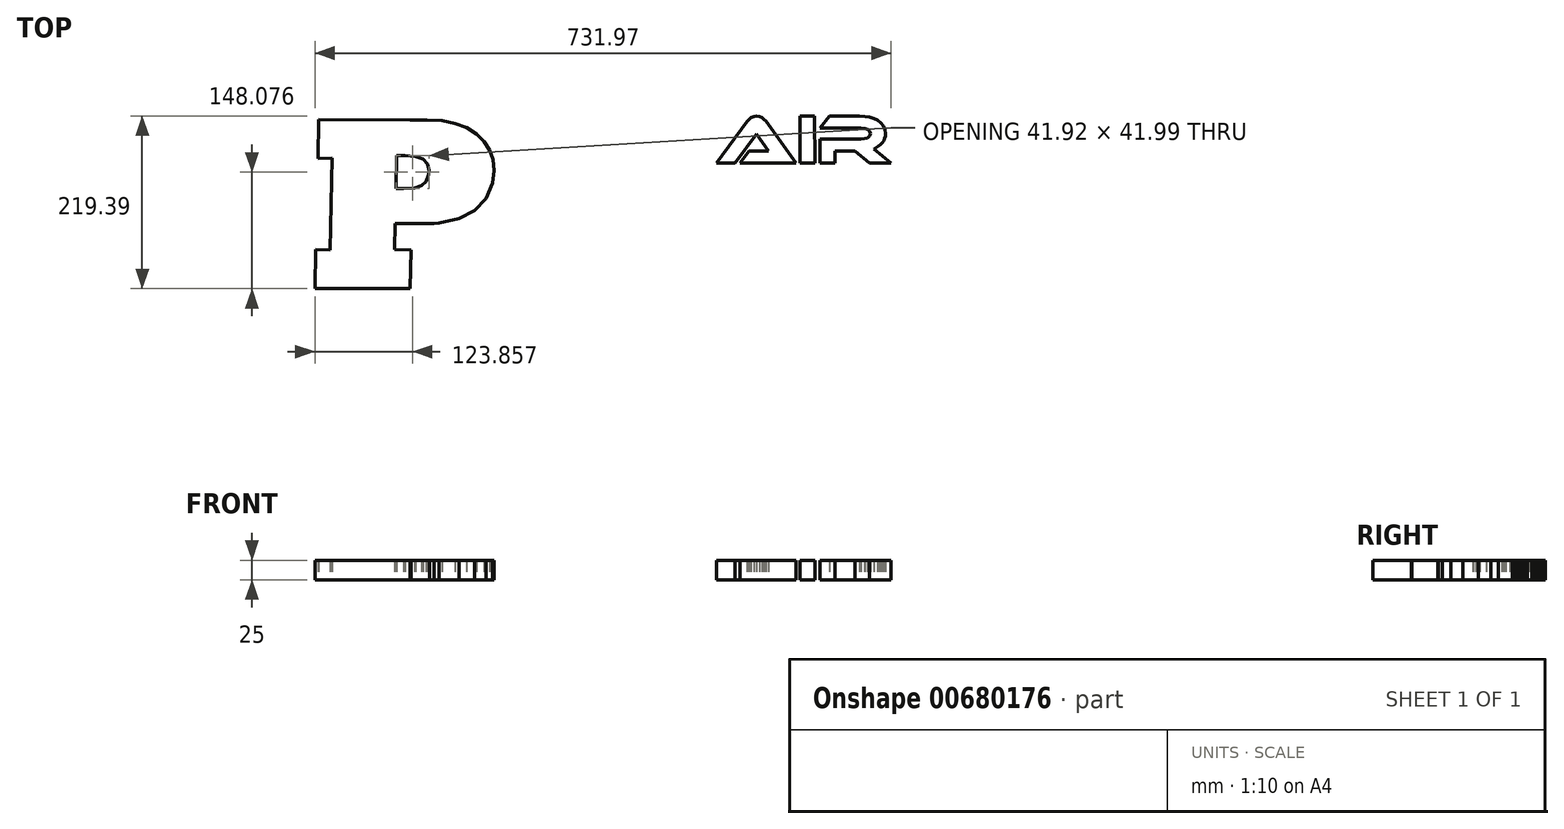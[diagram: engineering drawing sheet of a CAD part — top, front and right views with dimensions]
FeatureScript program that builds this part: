
annotation { "Feature Type Name" : "Feature", "Feature Type Description" : "" }
export const myFeature = defineFeature(function(context is Context, id is Id, definition is map)
    precondition{}
    {
        {
            var Q0;
            Q0=qCreatedBy(makeId("Top.planeOp"),FACE);
            var sketch = newSketch(context, id + "F0", { "sketchPlane" : qUnion([Q0])});
            skLineSegment(sketch, "E0", {"start": v(-203.38, -26.16) * mm, "end": v(-216.72, -33.2) * mm});
            skLineSegment(sketch, "E1", {"start": v(-216.72, -33.2) * mm, "end": v(-220.89, -34.75) * mm});
            skLineSegment(sketch, "E2", {"start": v(-220.89, -34.75) * mm, "end": v(-222.57, -34.45) * mm});
            skLineSegment(sketch, "E3", {"start": v(-222.57, -34.45) * mm, "end": v(-223.75, -33.54) * mm});
            skLineSegment(sketch, "E4", {"start": v(-223.75, -33.54) * mm, "end": v(-224.45, -31.99) * mm});
            skLineSegment(sketch, "E5", {"start": v(-224.45, -31.99) * mm, "end": v(-224.7, -29.77) * mm});
            skLineSegment(sketch, "E6", {"start": v(-224.7, -29.77) * mm, "end": v(-223.55, -23.02) * mm});
            skLineSegment(sketch, "E7", {"start": v(-223.55, -23.02) * mm, "end": v(-222.25, -19.7) * mm});
            skLineSegment(sketch, "E8", {"start": v(-222.25, -19.7) * mm, "end": v(-220.75, -17.4) * mm});
            skLineSegment(sketch, "E9", {"start": v(-220.75, -17.4) * mm, "end": v(-217.97, -15.19) * mm});
            skLineSegment(sketch, "E10", {"start": v(-217.97, -15.19) * mm, "end": v(-212.93, -12.27) * mm});
            skLineSegment(sketch, "E11", {"start": v(-212.93, -12.27) * mm, "end": v(-198.07, -5.72) * mm});
            skLineSegment(sketch, "E12", {"start": v(-198.07, -5.72) * mm, "end": v(-189.18, -2.7) * mm});
            skLineSegment(sketch, "E13", {"start": v(-189.18, -2.7) * mm, "end": v(-179.92, -0.26) * mm});
            skLineSegment(sketch, "E14", {"start": v(-179.92, -0.26) * mm, "end": v(-170.86, 1.37) * mm});
            skLineSegment(sketch, "E15", {"start": v(-170.86, 1.37) * mm, "end": v(-162.6, 1.92) * mm});
            skLineSegment(sketch, "E16", {"start": v(-162.6, 1.92) * mm, "end": v(-157.82, 1.48) * mm});
            skLineSegment(sketch, "E17", {"start": v(-157.82, 1.48) * mm, "end": v(-154.45, 0.18) * mm});
            skLineSegment(sketch, "E18", {"start": v(-154.45, 0.18) * mm, "end": v(-153.29, -1.05) * mm});
            skLineSegment(sketch, "E19", {"start": v(-153.29, -1.05) * mm, "end": v(-152.43, -2.99) * mm});
            skLineSegment(sketch, "E20", {"start": v(-152.43, -2.99) * mm, "end": v(-151.67, -9) * mm});
            skLineSegment(sketch, "E21", {"start": v(-151.67, -9) * mm, "end": v(-152.3, -13.27) * mm});
            skLineSegment(sketch, "E22", {"start": v(-152.3, -13.27) * mm, "end": v(-154.3, -17.99) * mm});
            skLineSegment(sketch, "E23", {"start": v(-154.3, -17.99) * mm, "end": v(-160.83, -27.6) * mm});
            skLineSegment(sketch, "E24", {"start": v(-160.83, -27.6) * mm, "end": v(-175.03, -44.15) * mm});
            skLineSegment(sketch, "E25", {"start": v(-175.03, -44.15) * mm, "end": v(-166.8, -43.03) * mm});
            skLineSegment(sketch, "E26", {"start": v(-166.8, -43.03) * mm, "end": v(-156.99, -41.97) * mm});
            skLineSegment(sketch, "E27", {"start": v(-156.99, -41.97) * mm, "end": v(-143.87, -22.9) * mm});
            skLineSegment(sketch, "E28", {"start": v(-143.87, -22.9) * mm, "end": v(-135.4, -11.09) * mm});
            skLineSegment(sketch, "E29", {"start": v(-135.4, -11.09) * mm, "end": v(-131.25, -5.72) * mm});
            skLineSegment(sketch, "E30", {"start": v(-131.25, -5.72) * mm, "end": v(-130.12, -4.73) * mm});
            skLineSegment(sketch, "E31", {"start": v(-130.12, -4.73) * mm, "end": v(-129.17, -4.63) * mm});
            skLineSegment(sketch, "E32", {"start": v(-129.17, -4.63) * mm, "end": v(-128.53, -5.44) * mm});
            skLineSegment(sketch, "E33", {"start": v(-128.53, -5.44) * mm, "end": v(-128.28, -7.2) * mm});
            skLineSegment(sketch, "E34", {"start": v(-128.28, -7.2) * mm, "end": v(-128.74, -11.37) * mm});
            skLineSegment(sketch, "E35", {"start": v(-128.74, -11.37) * mm, "end": v(-130.34, -14.57) * mm});
            skLineSegment(sketch, "E36", {"start": v(-130.34, -14.57) * mm, "end": v(-131.5, -16.28) * mm});
            skLineSegment(sketch, "E37", {"start": v(-131.5, -16.28) * mm, "end": v(-136.05, -23.27) * mm});
            skLineSegment(sketch, "E38", {"start": v(-136.05, -23.27) * mm, "end": v(-141.9, -31.82) * mm});
            skLineSegment(sketch, "E39", {"start": v(-141.9, -31.82) * mm, "end": v(-148.42, -41.85) * mm});
            skLineSegment(sketch, "E40", {"start": v(-148.42, -41.85) * mm, "end": v(-141.45, -42.42) * mm});
            skLineSegment(sketch, "E41", {"start": v(-141.45, -42.42) * mm, "end": v(-134.56, -43.65) * mm});
            skLineSegment(sketch, "E42", {"start": v(-134.56, -43.65) * mm, "end": v(-145.56, -58.86) * mm});
            skLineSegment(sketch, "E43", {"start": v(-145.56, -58.86) * mm, "end": v(-157.9, -58.24) * mm});
            skLineSegment(sketch, "E44", {"start": v(-157.9, -58.24) * mm, "end": v(-160.72, -64.1) * mm});
            skLineSegment(sketch, "E45", {"start": v(-160.72, -64.1) * mm, "end": v(-162.4, -68.13) * mm});
            skLineSegment(sketch, "E46", {"start": v(-162.4, -68.13) * mm, "end": v(-163.07, -71.66) * mm});
            skLineSegment(sketch, "E47", {"start": v(-163.07, -71.66) * mm, "end": v(-162.43, -74.31) * mm});
            skLineSegment(sketch, "E48", {"start": v(-162.43, -74.31) * mm, "end": v(-161.8, -76.22) * mm});
            skLineSegment(sketch, "E49", {"start": v(-161.8, -76.22) * mm, "end": v(-162.24, -77.5) * mm});
            skLineSegment(sketch, "E50", {"start": v(-162.24, -77.5) * mm, "end": v(-163.6, -78.88) * mm});
            skLineSegment(sketch, "E51", {"start": v(-163.6, -78.88) * mm, "end": v(-167.89, -81.34) * mm});
            skLineSegment(sketch, "E52", {"start": v(-167.89, -81.34) * mm, "end": v(-171.72, -82.4) * mm});
            skLineSegment(sketch, "E53", {"start": v(-171.72, -82.4) * mm, "end": v(-173.48, -81.53) * mm});
            skLineSegment(sketch, "E54", {"start": v(-173.48, -81.53) * mm, "end": v(-174.1, -78.9) * mm});
            skLineSegment(sketch, "E55", {"start": v(-174.1, -78.9) * mm, "end": v(-173.7, -74.93) * mm});
            skLineSegment(sketch, "E56", {"start": v(-173.7, -74.93) * mm, "end": v(-172.38, -70.24) * mm});
            skLineSegment(sketch, "E57", {"start": v(-172.38, -70.24) * mm, "end": v(-166.97, -58.74) * mm});
            skLineSegment(sketch, "E58", {"start": v(-166.97, -58.74) * mm, "end": v(-189.65, -61.67) * mm});
            skLineSegment(sketch, "E59", {"start": v(-189.65, -61.67) * mm, "end": v(-196.21, -70.9) * mm});
            skLineSegment(sketch, "E60", {"start": v(-196.21, -70.9) * mm, "end": v(-201.02, -78.28) * mm});
            skLineSegment(sketch, "E61", {"start": v(-201.02, -78.28) * mm, "end": v(-203.78, -82.28) * mm});
            skLineSegment(sketch, "E62", {"start": v(-203.78, -82.28) * mm, "end": v(-205.74, -83.28) * mm});
            skLineSegment(sketch, "E63", {"start": v(-205.74, -83.28) * mm, "end": v(-207.42, -82.89) * mm});
            skLineSegment(sketch, "E64", {"start": v(-207.42, -82.89) * mm, "end": v(-208.83, -81.72) * mm});
            skLineSegment(sketch, "E65", {"start": v(-208.83, -81.72) * mm, "end": v(-209.57, -80.47) * mm});
            skLineSegment(sketch, "E66", {"start": v(-209.57, -80.47) * mm, "end": v(-209.74, -79.1) * mm});
            skLineSegment(sketch, "E67", {"start": v(-209.74, -79.1) * mm, "end": v(-209.76, -77.78) * mm});
            skLineSegment(sketch, "E68", {"start": v(-209.76, -77.78) * mm, "end": v(-208.98, -75.6) * mm});
            skLineSegment(sketch, "E69", {"start": v(-208.98, -75.6) * mm, "end": v(-205.18, -69.88) * mm});
            skLineSegment(sketch, "E70", {"start": v(-205.18, -69.88) * mm, "end": v(-200.77, -63.42) * mm});
            skLineSegment(sketch, "E71", {"start": v(-200.77, -63.42) * mm, "end": v(-204.96, -63.6) * mm});
            skLineSegment(sketch, "E72", {"start": v(-204.96, -63.6) * mm, "end": v(-207.91, -63.3) * mm});
            skLineSegment(sketch, "E73", {"start": v(-207.91, -63.3) * mm, "end": v(-210.27, -62.42) * mm});
            skLineSegment(sketch, "E74", {"start": v(-210.27, -62.42) * mm, "end": v(-211.81, -61.1) * mm});
            skLineSegment(sketch, "E75", {"start": v(-211.81, -61.1) * mm, "end": v(-212.34, -59.49) * mm});
            skLineSegment(sketch, "E76", {"start": v(-212.34, -59.49) * mm, "end": v(-211.34, -55.21) * mm});
            skLineSegment(sketch, "E77", {"start": v(-211.34, -55.21) * mm, "end": v(-208.64, -51.41) * mm});
            skLineSegment(sketch, "E78", {"start": v(-208.64, -51.41) * mm, "end": v(-206.97, -50.27) * mm});
            skLineSegment(sketch, "E79", {"start": v(-206.97, -50.27) * mm, "end": v(-205.29, -49.88) * mm});
            skLineSegment(sketch, "E80", {"start": v(-205.29, -49.88) * mm, "end": v(-202.59, -50.57) * mm});
            skLineSegment(sketch, "E81", {"start": v(-202.59, -50.57) * mm, "end": v(-186.5, -46.58) * mm});
            skLineSegment(sketch, "E82", {"start": v(-186.5, -46.58) * mm, "end": v(-174.92, -33.54) * mm});
            skLineSegment(sketch, "E83", {"start": v(-174.92, -33.54) * mm, "end": v(-166.74, -23.55) * mm});
            skLineSegment(sketch, "E84", {"start": v(-166.74, -23.55) * mm, "end": v(-161.88, -16.6) * mm});
            skLineSegment(sketch, "E85", {"start": v(-161.88, -16.6) * mm, "end": v(-160.3, -12.67) * mm});
            skLineSegment(sketch, "E86", {"start": v(-160.3, -12.67) * mm, "end": v(-161.08, -10.4) * mm});
            skLineSegment(sketch, "E87", {"start": v(-161.08, -10.4) * mm, "end": v(-163.2, -9) * mm});
            skLineSegment(sketch, "E88", {"start": v(-163.2, -9) * mm, "end": v(-166.3, -8.51) * mm});
            skLineSegment(sketch, "E89", {"start": v(-166.3, -8.51) * mm, "end": v(-172.8, -9.63) * mm});
            skLineSegment(sketch, "E90", {"start": v(-172.8, -9.63) * mm, "end": v(-183.4, -12.92) * mm});
            skLineSegment(sketch, "E91", {"start": v(-183.4, -12.92) * mm, "end": v(-198.74, -18.95) * mm});
            skLineSegment(sketch, "E92", {"start": v(-198.74, -18.95) * mm, "end": v(-203.86, -21.24) * mm});
            skLineSegment(sketch, "E93", {"start": v(-203.86, -21.24) * mm, "end": v(-205.56, -22.5) * mm});
            skLineSegment(sketch, "E94", {"start": v(-205.56, -22.5) * mm, "end": v(-204.6, -23.61) * mm});
            skLineSegment(sketch, "E95", {"start": v(-204.6, -23.61) * mm, "end": v(-202.2, -23.99) * mm});
            skLineSegment(sketch, "E96", {"start": v(-202.2, -23.99) * mm, "end": v(-200.72, -24.42) * mm});
            skLineSegment(sketch, "E97", {"start": v(-200.72, -24.42) * mm, "end": v(-201.43, -25.1) * mm});
            skLineSegment(sketch, "E98", {"start": v(-201.43, -25.1) * mm, "end": v(-203.38, -26.16) * mm});
            skLineSegment(sketch, "E99", {"start": v(-126.25, -50.07) * mm, "end": v(-117.02, -42.58) * mm});
            skLineSegment(sketch, "E100", {"start": v(-117.02, -42.58) * mm, "end": v(-108.03, -37.3) * mm});
            skLineSegment(sketch, "E101", {"start": v(-108.03, -37.3) * mm, "end": v(-100.16, -34.17) * mm});
            skLineSegment(sketch, "E102", {"start": v(-100.16, -34.17) * mm, "end": v(-94.29, -33.13) * mm});
            skLineSegment(sketch, "E103", {"start": v(-94.29, -33.13) * mm, "end": v(-91.83, -34.22) * mm});
            skLineSegment(sketch, "E104", {"start": v(-91.83, -34.22) * mm, "end": v(-90, -36.74) * mm});
            skLineSegment(sketch, "E105", {"start": v(-90, -36.74) * mm, "end": v(-89.3, -38.86) * mm});
            skLineSegment(sketch, "E106", {"start": v(-89.3, -38.86) * mm, "end": v(-90.14, -40.5) * mm});
            skLineSegment(sketch, "E107", {"start": v(-90.14, -40.5) * mm, "end": v(-93.18, -41.78) * mm});
            skLineSegment(sketch, "E108", {"start": v(-93.18, -41.78) * mm, "end": v(-92, -44.34) * mm});
            skLineSegment(sketch, "E109", {"start": v(-92, -44.34) * mm, "end": v(-90.89, -46.86) * mm});
            skLineSegment(sketch, "E110", {"start": v(-90.89, -46.86) * mm, "end": v(-90.48, -48.58) * mm});
            skLineSegment(sketch, "E111", {"start": v(-90.48, -48.58) * mm, "end": v(-91.2, -50.72) * mm});
            skLineSegment(sketch, "E112", {"start": v(-91.2, -50.72) * mm, "end": v(-93.4, -54.16) * mm});
            skLineSegment(sketch, "E113", {"start": v(-93.4, -54.16) * mm, "end": v(-97.54, -60.18) * mm});
            skLineSegment(sketch, "E114", {"start": v(-97.54, -60.18) * mm, "end": v(-98.42, -62.33) * mm});
            skLineSegment(sketch, "E115", {"start": v(-98.42, -62.33) * mm, "end": v(-98.67, -64.92) * mm});
            skLineSegment(sketch, "E116", {"start": v(-98.67, -64.92) * mm, "end": v(-98.37, -66.94) * mm});
            skLineSegment(sketch, "E117", {"start": v(-98.37, -66.94) * mm, "end": v(-97.54, -68.38) * mm});
            skLineSegment(sketch, "E118", {"start": v(-97.54, -68.38) * mm, "end": v(-96.2, -69.25) * mm});
            skLineSegment(sketch, "E119", {"start": v(-96.2, -69.25) * mm, "end": v(-94.32, -69.54) * mm});
            skLineSegment(sketch, "E120", {"start": v(-94.32, -69.54) * mm, "end": v(-91.83, -69.03) * mm});
            skLineSegment(sketch, "E121", {"start": v(-91.83, -69.03) * mm, "end": v(-88.74, -67.5) * mm});
            skLineSegment(sketch, "E122", {"start": v(-80.77, -61.36) * mm, "end": v(-80.7, -65.17) * mm});
            skLineSegment(sketch, "E123", {"start": v(-87.9, -72.85) * mm, "end": v(-94.03, -78.33) * mm});
            skLineSegment(sketch, "E124", {"start": v(-94.03, -78.33) * mm, "end": v(-99.07, -81.63) * mm});
            skLineSegment(sketch, "E125", {"start": v(-99.07, -81.63) * mm, "end": v(-103.03, -82.72) * mm});
            skLineSegment(sketch, "E126", {"start": v(-103.03, -82.72) * mm, "end": v(-105.13, -82.33) * mm});
            skLineSegment(sketch, "E127", {"start": v(-105.13, -82.33) * mm, "end": v(-106.54, -81.13) * mm});
            skLineSegment(sketch, "E128", {"start": v(-106.54, -81.13) * mm, "end": v(-107.35, -79.15) * mm});
            skLineSegment(sketch, "E129", {"start": v(-107.35, -79.15) * mm, "end": v(-107.66, -76.41) * mm});
            skLineSegment(sketch, "E130", {"start": v(-107.66, -76.41) * mm, "end": v(-106.88, -70.37) * mm});
            skLineSegment(sketch, "E131", {"start": v(-106.88, -70.37) * mm, "end": v(-104.36, -62.11) * mm});
            skLineSegment(sketch, "E132", {"start": v(-104.36, -62.11) * mm, "end": v(-117.69, -76.5) * mm});
            skLineSegment(sketch, "E133", {"start": v(-117.69, -76.5) * mm, "end": v(-121.68, -79.72) * mm});
            skLineSegment(sketch, "E134", {"start": v(-121.68, -79.72) * mm, "end": v(-124.94, -80.79) * mm});
            skLineSegment(sketch, "E135", {"start": v(-124.94, -80.79) * mm, "end": v(-126.5, -80.2) * mm});
            skLineSegment(sketch, "E136", {"start": v(-126.5, -80.2) * mm, "end": v(-128.43, -78.4) * mm});
            skLineSegment(sketch, "E137", {"start": v(-128.43, -78.4) * mm, "end": v(-132.2, -72.26) * mm});
            skLineSegment(sketch, "E138", {"start": v(-132.2, -72.26) * mm, "end": v(-133.47, -68.4) * mm});
            skLineSegment(sketch, "E139", {"start": v(-133.47, -68.4) * mm, "end": v(-133.94, -64.42) * mm});
            skLineSegment(sketch, "E140", {"start": v(-133.94, -64.42) * mm, "end": v(-133.47, -59.52) * mm});
            skLineSegment(sketch, "E141", {"start": v(-133.47, -59.52) * mm, "end": v(-131.35, -55.5) * mm});
            skLineSegment(sketch, "E142", {"start": v(-131.35, -55.5) * mm, "end": v(-126.25, -50.07) * mm});
            skLineSegment(sketch, "E143", {"start": v(-96.4, -43.22) * mm, "end": v(-110.2, -50.07) * mm});
            skLineSegment(sketch, "E144", {"start": v(-110.2, -50.07) * mm, "end": v(-119.35, -55.8) * mm});
            skLineSegment(sketch, "E145", {"start": v(-119.35, -55.8) * mm, "end": v(-122.33, -58.42) * mm});
            skLineSegment(sketch, "E146", {"start": v(-122.33, -58.42) * mm, "end": v(-124.45, -61.06) * mm});
            skLineSegment(sketch, "E147", {"start": v(-124.45, -61.06) * mm, "end": v(-125.7, -63.75) * mm});
            skLineSegment(sketch, "E148", {"start": v(-125.7, -63.75) * mm, "end": v(-126.08, -66.48) * mm});
            skLineSegment(sketch, "E149", {"start": v(-126.08, -66.48) * mm, "end": v(-125.33, -69.76) * mm});
            skLineSegment(sketch, "E150", {"start": v(-125.33, -69.76) * mm, "end": v(-124.5, -70.72) * mm});
            skLineSegment(sketch, "E151", {"start": v(-124.5, -70.72) * mm, "end": v(-123.43, -71.04) * mm});
            skLineSegment(sketch, "E152", {"start": v(-123.43, -71.04) * mm, "end": v(-121, -70.16) * mm});
            skLineSegment(sketch, "E153", {"start": v(-121, -70.16) * mm, "end": v(-114.79, -65.7) * mm});
            skLineSegment(sketch, "E154", {"start": v(-114.79, -65.7) * mm, "end": v(-109.16, -60.08) * mm});
            skLineSegment(sketch, "E155", {"start": v(-109.16, -60.08) * mm, "end": v(-96.4, -43.22) * mm});
            skLineSegment(sketch, "E156", {"start": v(-39.37, -49.95) * mm, "end": v(-47.4, -60.32) * mm});
            skLineSegment(sketch, "E157", {"start": v(-47.4, -60.32) * mm, "end": v(-49.4, -64.11) * mm});
            skLineSegment(sketch, "E158", {"start": v(-49.4, -64.11) * mm, "end": v(-50.02, -66.98) * mm});
            skLineSegment(sketch, "E159", {"start": v(-50.02, -66.98) * mm, "end": v(-49.43, -69) * mm});
            skLineSegment(sketch, "E160", {"start": v(-49.43, -69) * mm, "end": v(-47.77, -69.67) * mm});
            skLineSegment(sketch, "E161", {"start": v(-47.77, -69.67) * mm, "end": v(-45.69, -69.2) * mm});
            skLineSegment(sketch, "E162", {"start": v(-45.69, -69.2) * mm, "end": v(-43.08, -67.76) * mm});
            skLineSegment(sketch, "E163", {"start": v(-34.12, -60.99) * mm, "end": v(-34.02, -65.3) * mm});
            skLineSegment(sketch, "E164", {"start": v(-47.4, -77.92) * mm, "end": v(-51.66, -80.82) * mm});
            skLineSegment(sketch, "E165", {"start": v(-51.66, -80.82) * mm, "end": v(-55.1, -81.8) * mm});
            skLineSegment(sketch, "E166", {"start": v(-55.1, -81.8) * mm, "end": v(-57.35, -81.37) * mm});
            skLineSegment(sketch, "E167", {"start": v(-57.35, -81.37) * mm, "end": v(-58.98, -80.1) * mm});
            skLineSegment(sketch, "E168", {"start": v(-58.98, -80.1) * mm, "end": v(-60, -78) * mm});
            skLineSegment(sketch, "E169", {"start": v(-60, -78) * mm, "end": v(-60.37, -75.04) * mm});
            skLineSegment(sketch, "E170", {"start": v(-60.37, -75.04) * mm, "end": v(-59.83, -71.1) * mm});
            skLineSegment(sketch, "E171", {"start": v(-59.83, -71.1) * mm, "end": v(-58.2, -67.08) * mm});
            skLineSegment(sketch, "E172", {"start": v(-58.2, -67.08) * mm, "end": v(-54.97, -61.08) * mm});
            skLineSegment(sketch, "E173", {"start": v(-54.97, -61.08) * mm, "end": v(-49.96, -52.26) * mm});
            skLineSegment(sketch, "E174", {"start": v(-49.96, -52.26) * mm, "end": v(-53.93, -54.95) * mm});
            skLineSegment(sketch, "E175", {"start": v(-53.93, -54.95) * mm, "end": v(-58.76, -59.43) * mm});
            skLineSegment(sketch, "E176", {"start": v(-58.76, -59.43) * mm, "end": v(-64.58, -65.83) * mm});
            skLineSegment(sketch, "E177", {"start": v(-64.58, -65.83) * mm, "end": v(-69.67, -72.57) * mm});
            skLineSegment(sketch, "E178", {"start": v(-69.67, -72.57) * mm, "end": v(-73.64, -77.57) * mm});
            skLineSegment(sketch, "E179", {"start": v(-73.64, -77.57) * mm, "end": v(-74.91, -78.53) * mm});
            skLineSegment(sketch, "E180", {"start": v(-74.91, -78.53) * mm, "end": v(-76.21, -78.85) * mm});
            skLineSegment(sketch, "E181", {"start": v(-76.21, -78.85) * mm, "end": v(-78.16, -77.8) * mm});
            skLineSegment(sketch, "E182", {"start": v(-78.16, -77.8) * mm, "end": v(-80, -74.66) * mm});
            skLineSegment(sketch, "E183", {"start": v(-80, -74.66) * mm, "end": v(-81.36, -70.13) * mm});
            skLineSegment(sketch, "E184", {"start": v(-81.21, -59.55) * mm, "end": v(-78.23, -54.06) * mm});
            skLineSegment(sketch, "E185", {"start": v(-78.23, -54.06) * mm, "end": v(-74.32, -48.33) * mm});
            skLineSegment(sketch, "E186", {"start": v(-74.32, -48.33) * mm, "end": v(-70.98, -44.37) * mm});
            skLineSegment(sketch, "E187", {"start": v(-70.98, -44.37) * mm, "end": v(-67.96, -42.06) * mm});
            skLineSegment(sketch, "E188", {"start": v(-67.96, -42.06) * mm, "end": v(-65.03, -41.29) * mm});
            skLineSegment(sketch, "E189", {"start": v(-65.03, -41.29) * mm, "end": v(-61.8, -41.97) * mm});
            skLineSegment(sketch, "E190", {"start": v(-61.8, -41.97) * mm, "end": v(-60.86, -42.84) * mm});
            skLineSegment(sketch, "E191", {"start": v(-60.86, -42.84) * mm, "end": v(-60.53, -44.09) * mm});
            skLineSegment(sketch, "E192", {"start": v(-60.53, -44.09) * mm, "end": v(-60.88, -45.4) * mm});
            skLineSegment(sketch, "E193", {"start": v(-60.88, -45.4) * mm, "end": v(-61.7, -46.64) * mm});
            skLineSegment(sketch, "E194", {"start": v(-61.7, -46.64) * mm, "end": v(-63.62, -48.83) * mm});
            skLineSegment(sketch, "E195", {"start": v(-63.62, -48.83) * mm, "end": v(-70.85, -57.82) * mm});
            skLineSegment(sketch, "E196", {"start": v(-70.85, -57.82) * mm, "end": v(-72.65, -60.88) * mm});
            skLineSegment(sketch, "E197", {"start": v(-72.65, -60.88) * mm, "end": v(-73.22, -62.99) * mm});
            skLineSegment(sketch, "E198", {"start": v(-73.22, -62.99) * mm, "end": v(-72.9, -64.34) * mm});
            skLineSegment(sketch, "E199", {"start": v(-72.9, -64.34) * mm, "end": v(-72, -64.8) * mm});
            skLineSegment(sketch, "E200", {"start": v(-72, -64.8) * mm, "end": v(-69.13, -62.4) * mm});
            skLineSegment(sketch, "E201", {"start": v(-69.13, -62.4) * mm, "end": v(-63.69, -56.1) * mm});
            skLineSegment(sketch, "E202", {"start": v(-63.69, -56.1) * mm, "end": v(-55.79, -47.95) * mm});
            skLineSegment(sketch, "E203", {"start": v(-55.79, -47.95) * mm, "end": v(-45.35, -39.8) * mm});
            skLineSegment(sketch, "E204", {"start": v(-45.35, -39.8) * mm, "end": v(-42.36, -38.06) * mm});
            skLineSegment(sketch, "E205", {"start": v(-42.36, -38.06) * mm, "end": v(-39.9, -37.49) * mm});
            skLineSegment(sketch, "E206", {"start": v(-39.9, -37.49) * mm, "end": v(-38.89, -38.17) * mm});
            skLineSegment(sketch, "E207", {"start": v(-38.89, -38.17) * mm, "end": v(-37.87, -40.23) * mm});
            skLineSegment(sketch, "E208", {"start": v(-37.87, -40.23) * mm, "end": v(-36.77, -45.77) * mm});
            skLineSegment(sketch, "E209", {"start": v(-36.77, -45.77) * mm, "end": v(-37.4, -47.5) * mm});
            skLineSegment(sketch, "E210", {"start": v(-37.4, -47.5) * mm, "end": v(-39.37, -49.95) * mm});
            skLineSegment(sketch, "E211", {"start": v(-4.98, -82.48) * mm, "end": v(-13.06, -95.7) * mm});
            skLineSegment(sketch, "E212", {"start": v(-13.06, -95.7) * mm, "end": v(-20.45, -105.11) * mm});
            skLineSegment(sketch, "E213", {"start": v(-20.45, -105.11) * mm, "end": v(-26.61, -110.73) * mm});
            skLineSegment(sketch, "E214", {"start": v(-26.61, -110.73) * mm, "end": v(-29.03, -112.13) * mm});
            skLineSegment(sketch, "E215", {"start": v(-29.03, -112.13) * mm, "end": v(-31.01, -112.6) * mm});
            skLineSegment(sketch, "E216", {"start": v(-31.01, -112.6) * mm, "end": v(-32.44, -112.02) * mm});
            skLineSegment(sketch, "E217", {"start": v(-32.44, -112.02) * mm, "end": v(-32.95, -110.28) * mm});
            skLineSegment(sketch, "E218", {"start": v(-32.95, -110.28) * mm, "end": v(-31.92, -105.14) * mm});
            skLineSegment(sketch, "E219", {"start": v(-31.92, -105.14) * mm, "end": v(-28.63, -98.75) * mm});
            skLineSegment(sketch, "E220", {"start": v(-28.63, -98.75) * mm, "end": v(-24.58, -93.37) * mm});
            skLineSegment(sketch, "E221", {"start": v(-24.58, -93.37) * mm, "end": v(-20.23, -88.83) * mm});
            skLineSegment(sketch, "E222", {"start": v(-20.23, -88.83) * mm, "end": v(-14.79, -84.08) * mm});
            skLineSegment(sketch, "E223", {"start": v(-14.79, -84.08) * mm, "end": v(-10.17, -80.17) * mm});
            skLineSegment(sketch, "E224", {"start": v(-10.17, -80.17) * mm, "end": v(-1.61, -60.68) * mm});
            skLineSegment(sketch, "E225", {"start": v(-1.61, -60.68) * mm, "end": v(-11.64, -70.92) * mm});
            skLineSegment(sketch, "E226", {"start": v(-11.64, -70.92) * mm, "end": v(-19.56, -77.07) * mm});
            skLineSegment(sketch, "E227", {"start": v(-19.56, -77.07) * mm, "end": v(-23, -78.7) * mm});
            skLineSegment(sketch, "E228", {"start": v(-23, -78.7) * mm, "end": v(-26.12, -79.23) * mm});
            skLineSegment(sketch, "E229", {"start": v(-26.12, -79.23) * mm, "end": v(-27.7, -78.91) * mm});
            skLineSegment(sketch, "E230", {"start": v(-27.7, -78.91) * mm, "end": v(-29.22, -77.96) * mm});
            skLineSegment(sketch, "E231", {"start": v(-29.22, -77.96) * mm, "end": v(-32.13, -74.14) * mm});
            skLineSegment(sketch, "E232", {"start": v(-32.13, -74.14) * mm, "end": v(-34.27, -68.97) * mm});
            skLineSegment(sketch, "E233", {"start": v(-34.02, -58.43) * mm, "end": v(-30.52, -52.57) * mm});
            skLineSegment(sketch, "E234", {"start": v(-30.52, -52.57) * mm, "end": v(-24.37, -46.18) * mm});
            skLineSegment(sketch, "E235", {"start": v(-24.37, -46.18) * mm, "end": v(-15.57, -39.8) * mm});
            skLineSegment(sketch, "E236", {"start": v(-15.57, -39.8) * mm, "end": v(-7.05, -35.26) * mm});
            skLineSegment(sketch, "E237", {"start": v(-7.05, -35.26) * mm, "end": v(-3.58, -34.13) * mm});
            skLineSegment(sketch, "E238", {"start": v(-3.58, -34.13) * mm, "end": v(-0.63, -33.75) * mm});
            skLineSegment(sketch, "E239", {"start": v(-0.63, -33.75) * mm, "end": v(2.4, -34.48) * mm});
            skLineSegment(sketch, "E240", {"start": v(2.4, -34.48) * mm, "end": v(3.17, -35.4) * mm});
            skLineSegment(sketch, "E241", {"start": v(3.17, -35.4) * mm, "end": v(3.45, -36.68) * mm});
            skLineSegment(sketch, "E242", {"start": v(3.45, -36.68) * mm, "end": v(2.95, -38.69) * mm});
            skLineSegment(sketch, "E243", {"start": v(2.95, -38.69) * mm, "end": v(1.37, -40.68) * mm});
            skLineSegment(sketch, "E244", {"start": v(1.37, -40.68) * mm, "end": v(-1.3, -42.64) * mm});
            skLineSegment(sketch, "E245", {"start": v(-1.3, -42.64) * mm, "end": v(-5.06, -44.59) * mm});
            skLineSegment(sketch, "E246", {"start": v(-5.06, -44.59) * mm, "end": v(-10.3, -47.27) * mm});
            skLineSegment(sketch, "E247", {"start": v(-10.3, -47.27) * mm, "end": v(-15.47, -50.7) * mm});
            skLineSegment(sketch, "E248", {"start": v(-15.47, -50.7) * mm, "end": v(-20.1, -54.62) * mm});
            skLineSegment(sketch, "E249", {"start": v(-20.1, -54.62) * mm, "end": v(-23.74, -58.77) * mm});
            skLineSegment(sketch, "E250", {"start": v(-23.74, -58.77) * mm, "end": v(-26.06, -62.84) * mm});
            skLineSegment(sketch, "E251", {"start": v(-26.06, -62.84) * mm, "end": v(-26.79, -66.48) * mm});
            skLineSegment(sketch, "E252", {"start": v(-26.79, -66.48) * mm, "end": v(-25.91, -69.17) * mm});
            skLineSegment(sketch, "E253", {"start": v(-25.91, -69.17) * mm, "end": v(-23.76, -70.17) * mm});
            skLineSegment(sketch, "E254", {"start": v(-23.76, -70.17) * mm, "end": v(-21.42, -69.67) * mm});
            skLineSegment(sketch, "E255", {"start": v(-21.42, -69.67) * mm, "end": v(-18.8, -68.17) * mm});
            skLineSegment(sketch, "E256", {"start": v(-18.8, -68.17) * mm, "end": v(-10.62, -61.12) * mm});
            skLineSegment(sketch, "E257", {"start": v(-10.62, -61.12) * mm, "end": v(-4.13, -53.66) * mm});
            skLineSegment(sketch, "E258", {"start": v(-4.13, -53.66) * mm, "end": v(2.57, -45.8) * mm});
            skLineSegment(sketch, "E259", {"start": v(2.57, -45.8) * mm, "end": v(5.11, -43.77) * mm});
            skLineSegment(sketch, "E260", {"start": v(5.11, -43.77) * mm, "end": v(7.42, -43.1) * mm});
            skLineSegment(sketch, "E261", {"start": v(7.42, -43.1) * mm, "end": v(9.47, -43.87) * mm});
            skLineSegment(sketch, "E262", {"start": v(9.47, -43.87) * mm, "end": v(10.31, -46.15) * mm});
            skLineSegment(sketch, "E263", {"start": v(10.31, -46.15) * mm, "end": v(9.83, -49.66) * mm});
            skLineSegment(sketch, "E264", {"start": v(9.83, -49.66) * mm, "end": v(8.23, -54.47) * mm});
            skLineSegment(sketch, "E265", {"start": v(8.23, -54.47) * mm, "end": v(0.42, -72.36) * mm});
            skLineSegment(sketch, "E266", {"start": v(15.32, -61.37) * mm, "end": v(15.42, -65.42) * mm});
            skLineSegment(sketch, "E267", {"start": v(21.93, -50.07) * mm, "end": v(31.12, -42.58) * mm});
            skLineSegment(sketch, "E268", {"start": v(31.12, -42.58) * mm, "end": v(40.08, -37.3) * mm});
            skLineSegment(sketch, "E269", {"start": v(40.08, -37.3) * mm, "end": v(47.93, -34.17) * mm});
            skLineSegment(sketch, "E270", {"start": v(47.93, -34.17) * mm, "end": v(53.8, -33.13) * mm});
            skLineSegment(sketch, "E271", {"start": v(53.8, -33.13) * mm, "end": v(56.27, -34.21) * mm});
            skLineSegment(sketch, "E272", {"start": v(56.27, -34.21) * mm, "end": v(58.12, -36.74) * mm});
            skLineSegment(sketch, "E273", {"start": v(58.12, -36.74) * mm, "end": v(58.83, -38.85) * mm});
            skLineSegment(sketch, "E274", {"start": v(58.83, -38.85) * mm, "end": v(58, -40.5) * mm});
            skLineSegment(sketch, "E275", {"start": v(58, -40.5) * mm, "end": v(54.97, -41.78) * mm});
            skLineSegment(sketch, "E276", {"start": v(54.97, -41.78) * mm, "end": v(56.16, -44.34) * mm});
            skLineSegment(sketch, "E277", {"start": v(56.16, -44.34) * mm, "end": v(57.3, -46.86) * mm});
            skLineSegment(sketch, "E278", {"start": v(57.3, -46.86) * mm, "end": v(57.71, -48.58) * mm});
            skLineSegment(sketch, "E279", {"start": v(57.71, -48.58) * mm, "end": v(57.01, -50.72) * mm});
            skLineSegment(sketch, "E280", {"start": v(57.01, -50.72) * mm, "end": v(54.82, -54.16) * mm});
            skLineSegment(sketch, "E281", {"start": v(54.82, -54.16) * mm, "end": v(50.72, -60.18) * mm});
            skLineSegment(sketch, "E282", {"start": v(50.72, -60.18) * mm, "end": v(49.86, -62.33) * mm});
            skLineSegment(sketch, "E283", {"start": v(49.86, -62.33) * mm, "end": v(49.63, -64.93) * mm});
            skLineSegment(sketch, "E284", {"start": v(49.63, -64.93) * mm, "end": v(49.94, -66.95) * mm});
            skLineSegment(sketch, "E285", {"start": v(49.94, -66.95) * mm, "end": v(50.78, -68.4) * mm});
            skLineSegment(sketch, "E286", {"start": v(50.78, -68.4) * mm, "end": v(52.14, -69.26) * mm});
            skLineSegment(sketch, "E287", {"start": v(52.14, -69.26) * mm, "end": v(54, -69.55) * mm});
            skLineSegment(sketch, "E288", {"start": v(54, -69.55) * mm, "end": v(56.5, -69.04) * mm});
            skLineSegment(sketch, "E289", {"start": v(56.5, -69.04) * mm, "end": v(59.58, -67.5) * mm});
            skLineSegment(sketch, "E290", {"start": v(67.62, -65.18) * mm, "end": v(60.46, -72.86) * mm});
            skLineSegment(sketch, "E291", {"start": v(60.46, -72.86) * mm, "end": v(54.37, -78.34) * mm});
            skLineSegment(sketch, "E292", {"start": v(54.37, -78.34) * mm, "end": v(49.34, -81.64) * mm});
            skLineSegment(sketch, "E293", {"start": v(49.34, -81.64) * mm, "end": v(45.39, -82.74) * mm});
            skLineSegment(sketch, "E294", {"start": v(45.39, -82.74) * mm, "end": v(43.28, -82.34) * mm});
            skLineSegment(sketch, "E295", {"start": v(43.28, -82.34) * mm, "end": v(41.87, -81.14) * mm});
            skLineSegment(sketch, "E296", {"start": v(41.87, -81.14) * mm, "end": v(41.04, -79.16) * mm});
            skLineSegment(sketch, "E297", {"start": v(41.04, -79.16) * mm, "end": v(40.7, -76.42) * mm});
            skLineSegment(sketch, "E298", {"start": v(40.7, -76.42) * mm, "end": v(41.45, -70.37) * mm});
            skLineSegment(sketch, "E299", {"start": v(41.45, -70.37) * mm, "end": v(43.91, -62.12) * mm});
            skLineSegment(sketch, "E300", {"start": v(43.91, -62.12) * mm, "end": v(30.68, -76.51) * mm});
            skLineSegment(sketch, "E301", {"start": v(30.68, -76.51) * mm, "end": v(26.7, -79.73) * mm});
            skLineSegment(sketch, "E302", {"start": v(26.7, -79.73) * mm, "end": v(23.45, -80.8) * mm});
            skLineSegment(sketch, "E303", {"start": v(23.45, -80.8) * mm, "end": v(21.88, -80.2) * mm});
            skLineSegment(sketch, "E304", {"start": v(21.88, -80.2) * mm, "end": v(19.94, -78.42) * mm});
            skLineSegment(sketch, "E305", {"start": v(19.94, -78.42) * mm, "end": v(16.12, -72.26) * mm});
            skLineSegment(sketch, "E306", {"start": v(16.12, -72.26) * mm, "end": v(14.83, -68.41) * mm});
            skLineSegment(sketch, "E307", {"start": v(14.77, -59.52) * mm, "end": v(16.87, -55.5) * mm});
            skLineSegment(sketch, "E308", {"start": v(16.87, -55.5) * mm, "end": v(21.93, -50.07) * mm});
            skLineSegment(sketch, "E309", {"start": v(51.75, -43.22) * mm, "end": v(37.99, -50.07) * mm});
            skLineSegment(sketch, "E310", {"start": v(37.99, -50.07) * mm, "end": v(28.87, -55.81) * mm});
            skLineSegment(sketch, "E311", {"start": v(28.87, -55.81) * mm, "end": v(25.9, -58.42) * mm});
            skLineSegment(sketch, "E312", {"start": v(25.9, -58.42) * mm, "end": v(23.81, -61.07) * mm});
            skLineSegment(sketch, "E313", {"start": v(23.81, -61.07) * mm, "end": v(22.58, -63.76) * mm});
            skLineSegment(sketch, "E314", {"start": v(22.58, -63.76) * mm, "end": v(22.22, -66.49) * mm});
            skLineSegment(sketch, "E315", {"start": v(22.22, -66.49) * mm, "end": v(22.99, -69.76) * mm});
            skLineSegment(sketch, "E316", {"start": v(22.99, -69.76) * mm, "end": v(23.83, -70.73) * mm});
            skLineSegment(sketch, "E317", {"start": v(23.83, -70.73) * mm, "end": v(24.9, -71.05) * mm});
            skLineSegment(sketch, "E318", {"start": v(24.9, -71.05) * mm, "end": v(27.32, -70.17) * mm});
            skLineSegment(sketch, "E319", {"start": v(27.32, -70.17) * mm, "end": v(33.5, -65.71) * mm});
            skLineSegment(sketch, "E320", {"start": v(33.5, -65.71) * mm, "end": v(39.1, -60.09) * mm});
            skLineSegment(sketch, "E321", {"start": v(39.1, -60.09) * mm, "end": v(51.75, -43.22) * mm});
            skLineSegment(sketch, "E322", {"start": v(66.34, -62) * mm, "end": v(71.3, -55.19) * mm});
            skLineSegment(sketch, "E323", {"start": v(71.3, -55.19) * mm, "end": v(68.34, -53.5) * mm});
            skLineSegment(sketch, "E324", {"start": v(68.34, -53.5) * mm, "end": v(67.62, -52.26) * mm});
            skLineSegment(sketch, "E325", {"start": v(67.62, -52.26) * mm, "end": v(67.35, -50.51) * mm});
            skLineSegment(sketch, "E326", {"start": v(67.35, -50.51) * mm, "end": v(67.75, -47.97) * mm});
            skLineSegment(sketch, "E327", {"start": v(67.75, -47.97) * mm, "end": v(69.07, -44.84) * mm});
            skLineSegment(sketch, "E328", {"start": v(69.07, -44.84) * mm, "end": v(73.53, -38.42) * mm});
            skLineSegment(sketch, "E329", {"start": v(73.53, -38.42) * mm, "end": v(76.1, -35.96) * mm});
            skLineSegment(sketch, "E330", {"start": v(76.1, -35.96) * mm, "end": v(78.43, -34.56) * mm});
            skLineSegment(sketch, "E331", {"start": v(78.43, -34.56) * mm, "end": v(80.11, -34.12) * mm});
            skLineSegment(sketch, "E332", {"start": v(80.11, -34.12) * mm, "end": v(81.06, -34.42) * mm});
            skLineSegment(sketch, "E333", {"start": v(81.06, -34.42) * mm, "end": v(81.4, -35.3) * mm});
            skLineSegment(sketch, "E334", {"start": v(81.4, -35.3) * mm, "end": v(79.57, -39.6) * mm});
            skLineSegment(sketch, "E335", {"start": v(79.57, -39.6) * mm, "end": v(95.8, -37.6) * mm});
            skLineSegment(sketch, "E336", {"start": v(95.8, -37.6) * mm, "end": v(97.62, -37.86) * mm});
            skLineSegment(sketch, "E337", {"start": v(97.62, -37.86) * mm, "end": v(99.45, -40.47) * mm});
            skLineSegment(sketch, "E338", {"start": v(99.45, -40.47) * mm, "end": v(100.25, -44.59) * mm});
            skLineSegment(sketch, "E339", {"start": v(100.25, -44.59) * mm, "end": v(99.17, -47.42) * mm});
            skLineSegment(sketch, "E340", {"start": v(99.17, -47.42) * mm, "end": v(95.32, -51.88) * mm});
            skLineSegment(sketch, "E341", {"start": v(95.32, -51.88) * mm, "end": v(92.37, -55.6) * mm});
            skLineSegment(sketch, "E342", {"start": v(92.37, -55.6) * mm, "end": v(89.97, -59.62) * mm});
            skLineSegment(sketch, "E343", {"start": v(89.97, -59.62) * mm, "end": v(88.38, -63.29) * mm});
            skLineSegment(sketch, "E344", {"start": v(88.38, -63.29) * mm, "end": v(87.89, -65.93) * mm});
            skLineSegment(sketch, "E345", {"start": v(87.89, -65.93) * mm, "end": v(88.86, -68.13) * mm});
            skLineSegment(sketch, "E346", {"start": v(88.86, -68.13) * mm, "end": v(91.6, -68.86) * mm});
            skLineSegment(sketch, "E347", {"start": v(91.6, -68.86) * mm, "end": v(93.85, -68.38) * mm});
            skLineSegment(sketch, "E348", {"start": v(93.85, -68.38) * mm, "end": v(96.78, -66.93) * mm});
            skLineSegment(sketch, "E349", {"start": v(96.78, -66.93) * mm, "end": v(104.67, -61.12) * mm});
            skLineSegment(sketch, "E350", {"start": v(104.67, -61.12) * mm, "end": v(104.8, -65.3) * mm});
            skLineSegment(sketch, "E351", {"start": v(104.8, -65.3) * mm, "end": v(96.45, -73.86) * mm});
            skLineSegment(sketch, "E352", {"start": v(96.45, -73.86) * mm, "end": v(90.32, -78.83) * mm});
            skLineSegment(sketch, "E353", {"start": v(90.32, -78.83) * mm, "end": v(87.63, -80.21) * mm});
            skLineSegment(sketch, "E354", {"start": v(87.63, -80.21) * mm, "end": v(85.22, -80.68) * mm});
            skLineSegment(sketch, "E355", {"start": v(85.22, -80.68) * mm, "end": v(82.8, -80.07) * mm});
            skLineSegment(sketch, "E356", {"start": v(82.8, -80.07) * mm, "end": v(80.77, -78.27) * mm});
            skLineSegment(sketch, "E357", {"start": v(80.77, -78.27) * mm, "end": v(79.37, -75.32) * mm});
            skLineSegment(sketch, "E358", {"start": v(79.37, -75.32) * mm, "end": v(78.82, -71.3) * mm});
            skLineSegment(sketch, "E359", {"start": v(78.82, -71.3) * mm, "end": v(79.08, -68.42) * mm});
            skLineSegment(sketch, "E360", {"start": v(79.08, -68.42) * mm, "end": v(80.03, -65.18) * mm});
            skLineSegment(sketch, "E361", {"start": v(80.03, -65.18) * mm, "end": v(83.86, -57.72) * mm});
            skLineSegment(sketch, "E362", {"start": v(83.86, -57.72) * mm, "end": v(89.62, -49.7) * mm});
            skLineSegment(sketch, "E363", {"start": v(89.62, -49.7) * mm, "end": v(85.7, -50.48) * mm});
            skLineSegment(sketch, "E364", {"start": v(77.35, -52) * mm, "end": v(72.79, -59.39) * mm});
            skLineSegment(sketch, "E365", {"start": v(150.83, -21.3) * mm, "end": v(150.67, -16.2) * mm});
            skLineSegment(sketch, "E366", {"start": v(150.67, -16.2) * mm, "end": v(155.12, -12.34) * mm});
            skLineSegment(sketch, "E367", {"start": v(155.12, -12.34) * mm, "end": v(160.15, -8.3) * mm});
            skLineSegment(sketch, "E368", {"start": v(160.15, -8.3) * mm, "end": v(165.9, -4.14) * mm});
            skLineSegment(sketch, "E369", {"start": v(165.9, -4.14) * mm, "end": v(172.68, -0.04) * mm});
            skLineSegment(sketch, "E370", {"start": v(172.68, -0.04) * mm, "end": v(175.41, -4.9) * mm});
            skLineSegment(sketch, "E371", {"start": v(175.41, -4.9) * mm, "end": v(176.42, -9.54) * mm});
            skLineSegment(sketch, "E372", {"start": v(176.42, -9.54) * mm, "end": v(175.53, -15.08) * mm});
            skLineSegment(sketch, "E373", {"start": v(175.53, -15.08) * mm, "end": v(172.85, -22.04) * mm});
            skLineSegment(sketch, "E374", {"start": v(172.85, -22.04) * mm, "end": v(168.56, -31.88) * mm});
            skLineSegment(sketch, "E375", {"start": v(168.56, -31.88) * mm, "end": v(162.57, -46.72) * mm});
            skLineSegment(sketch, "E376", {"start": v(162.57, -46.72) * mm, "end": v(158.35, -58.72) * mm});
            skLineSegment(sketch, "E377", {"start": v(158.35, -58.72) * mm, "end": v(155.87, -67.6) * mm});
            skLineSegment(sketch, "E378", {"start": v(155.87, -67.6) * mm, "end": v(155.13, -73.11) * mm});
            skLineSegment(sketch, "E379", {"start": v(155.13, -73.11) * mm, "end": v(155.64, -75.55) * mm});
            skLineSegment(sketch, "E380", {"start": v(155.64, -75.55) * mm, "end": v(156.18, -78.74) * mm});
            skLineSegment(sketch, "E381", {"start": v(156.18, -78.74) * mm, "end": v(155.96, -80.13) * mm});
            skLineSegment(sketch, "E382", {"start": v(155.96, -80.13) * mm, "end": v(155.2, -80.68) * mm});
            skLineSegment(sketch, "E383", {"start": v(155.2, -80.68) * mm, "end": v(152.26, -79.93) * mm});
            skLineSegment(sketch, "E384", {"start": v(152.26, -79.93) * mm, "end": v(148.16, -77.62) * mm});
            skLineSegment(sketch, "E385", {"start": v(148.16, -77.62) * mm, "end": v(145.66, -75.43) * mm});
            skLineSegment(sketch, "E386", {"start": v(145.66, -75.43) * mm, "end": v(144.37, -72.99) * mm});
            skLineSegment(sketch, "E387", {"start": v(144.37, -72.99) * mm, "end": v(143.86, -69.93) * mm});
            skLineSegment(sketch, "E388", {"start": v(143.86, -69.93) * mm, "end": v(144.74, -62.2) * mm});
            skLineSegment(sketch, "E389", {"start": v(144.74, -62.2) * mm, "end": v(147.74, -51.14) * mm});
            skLineSegment(sketch, "E390", {"start": v(147.74, -51.14) * mm, "end": v(152.6, -38.36) * mm});
            skLineSegment(sketch, "E391", {"start": v(152.6, -38.36) * mm, "end": v(158.88, -25.5) * mm});
            skLineSegment(sketch, "E392", {"start": v(158.88, -25.5) * mm, "end": v(165.41, -13.52) * mm});
            skLineSegment(sketch, "E393", {"start": v(165.41, -13.52) * mm, "end": v(158.28, -16.93) * mm});
            skLineSegment(sketch, "E394", {"start": v(158.28, -16.93) * mm, "end": v(150.83, -21.3) * mm});
            skLineSegment(sketch, "E395", {"start": v(193.03, -23.85) * mm, "end": v(190.39, -21.54) * mm});
            skLineSegment(sketch, "E396", {"start": v(190.39, -21.54) * mm, "end": v(189.5, -17.44) * mm});
            skLineSegment(sketch, "E397", {"start": v(189.5, -17.44) * mm, "end": v(190.42, -13.64) * mm});
            skLineSegment(sketch, "E398", {"start": v(190.42, -13.64) * mm, "end": v(193.46, -10.23) * mm});
            skLineSegment(sketch, "E399", {"start": v(193.46, -10.23) * mm, "end": v(198.41, -7.34) * mm});
            skLineSegment(sketch, "E400", {"start": v(198.41, -7.34) * mm, "end": v(205.1, -5.16) * mm});
            skLineSegment(sketch, "E401", {"start": v(205.1, -5.16) * mm, "end": v(213.15, -3.79) * mm});
            skLineSegment(sketch, "E402", {"start": v(213.15, -3.79) * mm, "end": v(222.12, -3.33) * mm});
            skLineSegment(sketch, "E403", {"start": v(222.12, -3.33) * mm, "end": v(230.97, -4.24) * mm});
            skLineSegment(sketch, "E404", {"start": v(230.97, -4.24) * mm, "end": v(234.48, -5.39) * mm});
            skLineSegment(sketch, "E405", {"start": v(234.48, -5.39) * mm, "end": v(237.38, -7) * mm});
            skLineSegment(sketch, "E406", {"start": v(237.38, -7) * mm, "end": v(239.67, -9.04) * mm});
            skLineSegment(sketch, "E407", {"start": v(239.67, -9.04) * mm, "end": v(241.34, -11.53) * mm});
            skLineSegment(sketch, "E408", {"start": v(241.34, -11.53) * mm, "end": v(242.4, -14.45) * mm});
            skLineSegment(sketch, "E409", {"start": v(242.4, -14.45) * mm, "end": v(242.83, -17.8) * mm});
            skLineSegment(sketch, "E410", {"start": v(242.83, -17.8) * mm, "end": v(242.5, -21.8) * mm});
            skLineSegment(sketch, "E411", {"start": v(242.5, -21.8) * mm, "end": v(241.18, -25.3) * mm});
            skLineSegment(sketch, "E412", {"start": v(241.18, -25.3) * mm, "end": v(238.77, -28.44) * mm});
            skLineSegment(sketch, "E413", {"start": v(238.77, -28.44) * mm, "end": v(235.1, -31.31) * mm});
            skLineSegment(sketch, "E414", {"start": v(235.1, -31.31) * mm, "end": v(231.28, -32.98) * mm});
            skLineSegment(sketch, "E415", {"start": v(231.28, -32.98) * mm, "end": v(224.58, -34.99) * mm});
            skLineSegment(sketch, "E416", {"start": v(224.58, -34.99) * mm, "end": v(202.58, -40.04) * mm});
            skLineSegment(sketch, "E417", {"start": v(202.58, -40.04) * mm, "end": v(210.42, -40.99) * mm});
            skLineSegment(sketch, "E418", {"start": v(210.42, -40.99) * mm, "end": v(217, -42.34) * mm});
            skLineSegment(sketch, "E419", {"start": v(217, -42.34) * mm, "end": v(222.35, -44.34) * mm});
            skLineSegment(sketch, "E420", {"start": v(222.35, -44.34) * mm, "end": v(226.53, -47.2) * mm});
            skLineSegment(sketch, "E421", {"start": v(226.53, -47.2) * mm, "end": v(229.28, -51.09) * mm});
            skLineSegment(sketch, "E422", {"start": v(229.28, -51.09) * mm, "end": v(230.32, -56.13) * mm});
            skLineSegment(sketch, "E423", {"start": v(230.32, -56.13) * mm, "end": v(230.09, -59.18) * mm});
            skLineSegment(sketch, "E424", {"start": v(230.09, -59.18) * mm, "end": v(229.19, -62.23) * mm});
            skLineSegment(sketch, "E425", {"start": v(229.19, -62.23) * mm, "end": v(225.38, -68.3) * mm});
            skLineSegment(sketch, "E426", {"start": v(225.38, -68.3) * mm, "end": v(219.14, -73.83) * mm});
            skLineSegment(sketch, "E427", {"start": v(219.14, -73.83) * mm, "end": v(210.75, -78.28) * mm});
            skLineSegment(sketch, "E428", {"start": v(210.75, -78.28) * mm, "end": v(200.71, -81.2) * mm});
            skLineSegment(sketch, "E429", {"start": v(200.71, -81.2) * mm, "end": v(189.54, -82.18) * mm});
            skLineSegment(sketch, "E430", {"start": v(189.54, -82.18) * mm, "end": v(182.06, -81.53) * mm});
            skLineSegment(sketch, "E431", {"start": v(182.06, -81.53) * mm, "end": v(176.4, -79.59) * mm});
            skLineSegment(sketch, "E432", {"start": v(176.4, -79.59) * mm, "end": v(172.83, -76.64) * mm});
            skLineSegment(sketch, "E433", {"start": v(172.83, -76.64) * mm, "end": v(171.9, -74.9) * mm});
            skLineSegment(sketch, "E434", {"start": v(171.9, -74.9) * mm, "end": v(171.56, -73) * mm});
            skLineSegment(sketch, "E435", {"start": v(171.56, -73) * mm, "end": v(171.86, -70.6) * mm});
            skLineSegment(sketch, "E436", {"start": v(171.86, -70.6) * mm, "end": v(172.9, -68.09) * mm});
            skLineSegment(sketch, "E437", {"start": v(172.9, -68.09) * mm, "end": v(176.34, -63.62) * mm});
            skLineSegment(sketch, "E438", {"start": v(176.34, -63.62) * mm, "end": v(178.2, -62.21) * mm});
            skLineSegment(sketch, "E439", {"start": v(178.2, -62.21) * mm, "end": v(179.79, -61.75) * mm});
            skLineSegment(sketch, "E440", {"start": v(179.79, -61.75) * mm, "end": v(180.69, -62.37) * mm});
            skLineSegment(sketch, "E441", {"start": v(180.69, -62.37) * mm, "end": v(180.11, -64.06) * mm});
            skLineSegment(sketch, "E442", {"start": v(180.11, -64.06) * mm, "end": v(179.53, -65.43) * mm});
            skLineSegment(sketch, "E443", {"start": v(179.53, -65.43) * mm, "end": v(180.3, -66.82) * mm});
            skLineSegment(sketch, "E444", {"start": v(180.3, -66.82) * mm, "end": v(182.53, -68) * mm});
            skLineSegment(sketch, "E445", {"start": v(182.53, -68) * mm, "end": v(185.89, -68.79) * mm});
            skLineSegment(sketch, "E446", {"start": v(185.89, -68.79) * mm, "end": v(190.06, -69.05) * mm});
            skLineSegment(sketch, "E447", {"start": v(190.06, -69.05) * mm, "end": v(196.22, -68.7) * mm});
            skLineSegment(sketch, "E448", {"start": v(196.22, -68.7) * mm, "end": v(202.18, -67.65) * mm});
            skLineSegment(sketch, "E449", {"start": v(202.18, -67.65) * mm, "end": v(207.71, -66.02) * mm});
            skLineSegment(sketch, "E450", {"start": v(207.71, -66.02) * mm, "end": v(212.62, -63.96) * mm});
            skLineSegment(sketch, "E451", {"start": v(212.62, -63.96) * mm, "end": v(216.73, -61.61) * mm});
            skLineSegment(sketch, "E452", {"start": v(216.73, -61.61) * mm, "end": v(219.86, -59.12) * mm});
            skLineSegment(sketch, "E453", {"start": v(219.86, -59.12) * mm, "end": v(221.82, -56.67) * mm});
            skLineSegment(sketch, "E454", {"start": v(221.82, -56.67) * mm, "end": v(222.43, -54.44) * mm});
            skLineSegment(sketch, "E455", {"start": v(222.43, -54.44) * mm, "end": v(222.01, -52.46) * mm});
            skLineSegment(sketch, "E456", {"start": v(222.01, -52.46) * mm, "end": v(220.92, -50.82) * mm});
            skLineSegment(sketch, "E457", {"start": v(220.92, -50.82) * mm, "end": v(219.14, -49.53) * mm});
            skLineSegment(sketch, "E458", {"start": v(219.14, -49.53) * mm, "end": v(216.68, -48.58) * mm});
            skLineSegment(sketch, "E459", {"start": v(216.68, -48.58) * mm, "end": v(209.68, -47.4) * mm});
            skLineSegment(sketch, "E460", {"start": v(209.68, -47.4) * mm, "end": v(199.87, -47.02) * mm});
            skLineSegment(sketch, "E461", {"start": v(199.87, -47.02) * mm, "end": v(192.52, -47.67) * mm});
            skLineSegment(sketch, "E462", {"start": v(192.52, -47.67) * mm, "end": v(189.13, -48.33) * mm});
            skLineSegment(sketch, "E463", {"start": v(189.13, -48.33) * mm, "end": v(188.41, -47.94) * mm});
            skLineSegment(sketch, "E464", {"start": v(188.41, -47.94) * mm, "end": v(188.14, -46.77) * mm});
            skLineSegment(sketch, "E465", {"start": v(188.14, -46.77) * mm, "end": v(189.28, -40.54) * mm});
            skLineSegment(sketch, "E466", {"start": v(189.28, -40.54) * mm, "end": v(190.65, -37.39) * mm});
            skLineSegment(sketch, "E467", {"start": v(190.65, -37.39) * mm, "end": v(192.28, -35.55) * mm});
            skLineSegment(sketch, "E468", {"start": v(192.28, -35.55) * mm, "end": v(200.95, -33.5) * mm});
            skLineSegment(sketch, "E469", {"start": v(200.95, -33.5) * mm, "end": v(213.96, -31.03) * mm});
            skLineSegment(sketch, "E470", {"start": v(213.96, -31.03) * mm, "end": v(226.88, -27.14) * mm});
            skLineSegment(sketch, "E471", {"start": v(226.88, -27.14) * mm, "end": v(230.97, -25.19) * mm});
            skLineSegment(sketch, "E472", {"start": v(230.97, -25.19) * mm, "end": v(233.87, -22.94) * mm});
            skLineSegment(sketch, "E473", {"start": v(233.87, -22.94) * mm, "end": v(235.58, -20.66) * mm});
            skLineSegment(sketch, "E474", {"start": v(235.58, -20.66) * mm, "end": v(236.1, -18.62) * mm});
            skLineSegment(sketch, "E475", {"start": v(236.1, -18.62) * mm, "end": v(235.27, -16.5) * mm});
            skLineSegment(sketch, "E476", {"start": v(235.27, -16.5) * mm, "end": v(232.95, -14.98) * mm});
            skLineSegment(sketch, "E477", {"start": v(232.95, -14.98) * mm, "end": v(229.15, -14.07) * mm});
            skLineSegment(sketch, "E478", {"start": v(229.15, -14.07) * mm, "end": v(223.85, -13.77) * mm});
            skLineSegment(sketch, "E479", {"start": v(223.85, -13.77) * mm, "end": v(212.43, -14.48) * mm});
            skLineSegment(sketch, "E480", {"start": v(212.43, -14.48) * mm, "end": v(203.76, -16.22) * mm});
            skLineSegment(sketch, "E481", {"start": v(203.76, -16.22) * mm, "end": v(201.42, -17.23) * mm});
            skLineSegment(sketch, "E482", {"start": v(201.42, -17.23) * mm, "end": v(200.66, -18.18) * mm});
            skLineSegment(sketch, "E483", {"start": v(200.66, -18.18) * mm, "end": v(201.36, -19.49) * mm});
            skLineSegment(sketch, "E484", {"start": v(201.36, -19.49) * mm, "end": v(202.7, -20.24) * mm});
            skLineSegment(sketch, "E485", {"start": v(202.7, -20.24) * mm, "end": v(204.89, -20.98) * mm});
            skLineSegment(sketch, "E486", {"start": v(204.89, -20.98) * mm, "end": v(205.66, -21.51) * mm});
            skLineSegment(sketch, "E487", {"start": v(205.66, -21.51) * mm, "end": v(206.06, -22.41) * mm});
            skLineSegment(sketch, "E488", {"start": v(206.06, -22.41) * mm, "end": v(205.27, -23.16) * mm});
            skLineSegment(sketch, "E489", {"start": v(205.27, -23.16) * mm, "end": v(202.83, -23.64) * mm});
            skLineSegment(sketch, "E490", {"start": v(202.83, -23.64) * mm, "end": v(193.03, -23.85) * mm});
            skLineSegment(sketch, "E491", {"start": v(-486.7, 114.34) * mm, "end": v(-475.43, 129.85) * mm});
            skLineSegment(sketch, "E492", {"start": v(-475.43, 129.85) * mm, "end": v(-450.22, 129.85) * mm});
            skLineSegment(sketch, "E493", {"start": v(-450.22, 129.85) * mm, "end": v(-465.94, 151.3) * mm});
            skLineSegment(sketch, "E494", {"start": v(-465.94, 151.3) * mm, "end": v(-493.07, 114.34) * mm});
            skLineSegment(sketch, "E495", {"start": v(-493.07, 114.34) * mm, "end": v(-516.27, 114.33) * mm});
            skLineSegment(sketch, "E496", {"start": v(-516.27, 114.33) * mm, "end": v(-477.69, 167.4) * mm});
            skLineSegment(sketch, "E497", {"start": v(-477.69, 167.4) * mm, "end": v(-475.5, 169.88) * mm});
            skLineSegment(sketch, "E498", {"start": v(-475.5, 169.88) * mm, "end": v(-472.6, 172.03) * mm});
            skLineSegment(sketch, "E499", {"start": v(-472.6, 172.03) * mm, "end": v(-469.08, 173.64) * mm});
            skLineSegment(sketch, "E500", {"start": v(-469.08, 173.64) * mm, "end": v(-465.67, 174.18) * mm});
            skLineSegment(sketch, "E501", {"start": v(-465.67, 174.18) * mm, "end": v(-462.22, 173.65) * mm});
            skLineSegment(sketch, "E502", {"start": v(-462.22, 173.65) * mm, "end": v(-458.73, 172.04) * mm});
            skLineSegment(sketch, "E503", {"start": v(-458.73, 172.04) * mm, "end": v(-455.92, 169.93) * mm});
            skLineSegment(sketch, "E504", {"start": v(-455.92, 169.93) * mm, "end": v(-453.7, 167.42) * mm});
            skLineSegment(sketch, "E505", {"start": v(-453.7, 167.42) * mm, "end": v(-415.73, 114.36) * mm});
            skLineSegment(sketch, "E506", {"start": v(-415.73, 114.36) * mm, "end": v(-486.7, 114.34) * mm});
            skLineSegment(sketch, "E507", {"start": v(-391.65, 114.36) * mm, "end": v(-410.35, 114.36) * mm});
            skLineSegment(sketch, "E508", {"start": v(-410.35, 114.36) * mm, "end": v(-410.67, 174.04) * mm});
            skLineSegment(sketch, "E509", {"start": v(-410.67, 174.04) * mm, "end": v(-392.02, 174.05) * mm});
            skLineSegment(sketch, "E510", {"start": v(-392.02, 174.05) * mm, "end": v(-391.65, 114.36) * mm});
            skLineSegment(sketch, "E511", {"start": v(-294.7, 114.39) * mm, "end": v(-321.95, 114.38) * mm});
            skLineSegment(sketch, "E512", {"start": v(-321.95, 114.38) * mm, "end": v(-340.35, 129.4) * mm});
            skLineSegment(sketch, "E513", {"start": v(-340.35, 129.4) * mm, "end": v(-366.14, 129.4) * mm});
            skLineSegment(sketch, "E514", {"start": v(-366.14, 129.4) * mm, "end": v(-366.03, 114.37) * mm});
            skLineSegment(sketch, "E515", {"start": v(-366.03, 114.37) * mm, "end": v(-384.82, 114.37) * mm});
            skLineSegment(sketch, "E516", {"start": v(-384.82, 114.37) * mm, "end": v(-385.02, 144.88) * mm});
            skLineSegment(sketch, "E517", {"start": v(-385.02, 144.88) * mm, "end": v(-332.94, 144.9) * mm});
            skLineSegment(sketch, "E518", {"start": v(-332.94, 144.9) * mm, "end": v(-328.59, 145.25) * mm});
            skLineSegment(sketch, "E519", {"start": v(-328.59, 145.25) * mm, "end": v(-325.08, 146.3) * mm});
            skLineSegment(sketch, "E520", {"start": v(-325.08, 146.3) * mm, "end": v(-323.37, 147.32) * mm});
            skLineSegment(sketch, "E521", {"start": v(-323.37, 147.32) * mm, "end": v(-322.15, 148.56) * mm});
            skLineSegment(sketch, "E522", {"start": v(-322.15, 148.56) * mm, "end": v(-321.43, 150.01) * mm});
            skLineSegment(sketch, "E523", {"start": v(-321.43, 150.01) * mm, "end": v(-321.2, 151.68) * mm});
            skLineSegment(sketch, "E524", {"start": v(-321.2, 151.68) * mm, "end": v(-321.96, 154.72) * mm});
            skLineSegment(sketch, "E525", {"start": v(-321.96, 154.72) * mm, "end": v(-324.2, 156.9) * mm});
            skLineSegment(sketch, "E526", {"start": v(-324.2, 156.9) * mm, "end": v(-327.9, 158.2) * mm});
            skLineSegment(sketch, "E527", {"start": v(-327.9, 158.2) * mm, "end": v(-333.06, 158.62) * mm});
            skLineSegment(sketch, "E528", {"start": v(-333.06, 158.62) * mm, "end": v(-385.1, 158.6) * mm});
            skLineSegment(sketch, "E529", {"start": v(-385.1, 158.6) * mm, "end": v(-373, 174.06) * mm});
            skLineSegment(sketch, "E530", {"start": v(-373, 174.06) * mm, "end": v(-334.96, 174.07) * mm});
            skLineSegment(sketch, "E531", {"start": v(-334.96, 174.07) * mm, "end": v(-328.22, 173.74) * mm});
            skLineSegment(sketch, "E532", {"start": v(-328.22, 173.74) * mm, "end": v(-322.15, 172.76) * mm});
            skLineSegment(sketch, "E533", {"start": v(-322.15, 172.76) * mm, "end": v(-316.74, 171.1) * mm});
            skLineSegment(sketch, "E534", {"start": v(-316.74, 171.1) * mm, "end": v(-312, 168.8) * mm});
            skLineSegment(sketch, "E535", {"start": v(-312, 168.8) * mm, "end": v(-307.64, 165.46) * mm});
            skLineSegment(sketch, "E536", {"start": v(-307.64, 165.46) * mm, "end": v(-304.52, 161.48) * mm});
            skLineSegment(sketch, "E537", {"start": v(-304.52, 161.48) * mm, "end": v(-302.62, 156.87) * mm});
            skLineSegment(sketch, "E538", {"start": v(-302.62, 156.87) * mm, "end": v(-301.95, 151.6) * mm});
            skLineSegment(sketch, "E539", {"start": v(-301.95, 151.6) * mm, "end": v(-302.16, 148.53) * mm});
            skLineSegment(sketch, "E540", {"start": v(-302.16, 148.53) * mm, "end": v(-302.88, 145.61) * mm});
            skLineSegment(sketch, "E541", {"start": v(-302.88, 145.61) * mm, "end": v(-304.1, 142.84) * mm});
            skLineSegment(sketch, "E542", {"start": v(-304.1, 142.84) * mm, "end": v(-305.81, 140.22) * mm});
            skLineSegment(sketch, "E543", {"start": v(-305.81, 140.22) * mm, "end": v(-307.97, 137.82) * mm});
            skLineSegment(sketch, "E544", {"start": v(-307.97, 137.82) * mm, "end": v(-310.51, 135.71) * mm});
            skLineSegment(sketch, "E545", {"start": v(-310.51, 135.71) * mm, "end": v(-316.76, 132.38) * mm});
            skLineSegment(sketch, "E546", {"start": v(-316.76, 132.38) * mm, "end": v(-294.7, 114.39) * mm});
            skLineSegment(sketch, "E547", {"start": v(-178.14, 174.13) * mm, "end": v(-189.95, 158.68) * mm});
            skLineSegment(sketch, "E548", {"start": v(-189.95, 158.68) * mm, "end": v(-232.64, 158.66) * mm});
            skLineSegment(sketch, "E549", {"start": v(-232.64, 158.66) * mm, "end": v(-235.2, 158.06) * mm});
            skLineSegment(sketch, "E550", {"start": v(-235.2, 158.06) * mm, "end": v(-235.84, 157.3) * mm});
            skLineSegment(sketch, "E551", {"start": v(-235.84, 157.3) * mm, "end": v(-236.04, 156.26) * mm});
            skLineSegment(sketch, "E552", {"start": v(-236.04, 156.26) * mm, "end": v(-235.81, 155.2) * mm});
            skLineSegment(sketch, "E553", {"start": v(-235.81, 155.2) * mm, "end": v(-235.16, 154.46) * mm});
            skLineSegment(sketch, "E554", {"start": v(-235.16, 154.46) * mm, "end": v(-232.57, 153.86) * mm});
            skLineSegment(sketch, "E555", {"start": v(-232.57, 153.86) * mm, "end": v(-201.84, 153.87) * mm});
            skLineSegment(sketch, "E556", {"start": v(-201.84, 153.87) * mm, "end": v(-196.57, 153.54) * mm});
            skLineSegment(sketch, "E557", {"start": v(-196.57, 153.54) * mm, "end": v(-191.75, 152.55) * mm});
            skLineSegment(sketch, "E558", {"start": v(-191.75, 152.55) * mm, "end": v(-187.36, 150.9) * mm});
            skLineSegment(sketch, "E559", {"start": v(-187.36, 150.9) * mm, "end": v(-183.41, 148.58) * mm});
            skLineSegment(sketch, "E560", {"start": v(-183.41, 148.58) * mm, "end": v(-180.03, 145.56) * mm});
            skLineSegment(sketch, "E561", {"start": v(-180.03, 145.56) * mm, "end": v(-177.6, 142.12) * mm});
            skLineSegment(sketch, "E562", {"start": v(-177.6, 142.12) * mm, "end": v(-176.1, 138.27) * mm});
            skLineSegment(sketch, "E563", {"start": v(-176.1, 138.27) * mm, "end": v(-175.55, 134) * mm});
            skLineSegment(sketch, "E564", {"start": v(-175.55, 134) * mm, "end": v(-175.97, 129.78) * mm});
            skLineSegment(sketch, "E565", {"start": v(-175.97, 129.78) * mm, "end": v(-177.35, 125.98) * mm});
            skLineSegment(sketch, "E566", {"start": v(-177.35, 125.98) * mm, "end": v(-179.7, 122.6) * mm});
            skLineSegment(sketch, "E567", {"start": v(-179.7, 122.6) * mm, "end": v(-183.03, 119.65) * mm});
            skLineSegment(sketch, "E568", {"start": v(-183.03, 119.65) * mm, "end": v(-186.84, 117.36) * mm});
            skLineSegment(sketch, "E569", {"start": v(-186.84, 117.36) * mm, "end": v(-191.14, 115.73) * mm});
            skLineSegment(sketch, "E570", {"start": v(-191.14, 115.73) * mm, "end": v(-195.93, 114.74) * mm});
            skLineSegment(sketch, "E571", {"start": v(-195.93, 114.74) * mm, "end": v(-201.22, 114.42) * mm});
            skLineSegment(sketch, "E572", {"start": v(-201.22, 114.42) * mm, "end": v(-256.53, 114.4) * mm});
            skLineSegment(sketch, "E573", {"start": v(-256.53, 114.4) * mm, "end": v(-244.66, 129.84) * mm});
            skLineSegment(sketch, "E574", {"start": v(-244.66, 129.84) * mm, "end": v(-201.46, 129.85) * mm});
            skLineSegment(sketch, "E575", {"start": v(-201.46, 129.85) * mm, "end": v(-198.68, 130.1) * mm});
            skLineSegment(sketch, "E576", {"start": v(-198.68, 130.1) * mm, "end": v(-196.2, 130.85) * mm});
            skLineSegment(sketch, "E577", {"start": v(-196.2, 130.85) * mm, "end": v(-193.96, 132.32) * mm});
            skLineSegment(sketch, "E578", {"start": v(-193.96, 132.32) * mm, "end": v(-193.23, 134.24) * mm});
            skLineSegment(sketch, "E579", {"start": v(-193.23, 134.24) * mm, "end": v(-194.02, 136.21) * mm});
            skLineSegment(sketch, "E580", {"start": v(-194.02, 136.21) * mm, "end": v(-196.3, 137.64) * mm});
            skLineSegment(sketch, "E581", {"start": v(-196.3, 137.64) * mm, "end": v(-198.76, 138.26) * mm});
            skLineSegment(sketch, "E582", {"start": v(-198.76, 138.26) * mm, "end": v(-201.6, 138.47) * mm});
            skLineSegment(sketch, "E583", {"start": v(-201.6, 138.47) * mm, "end": v(-232.36, 138.46) * mm});
            skLineSegment(sketch, "E584", {"start": v(-232.36, 138.46) * mm, "end": v(-237.26, 138.75) * mm});
            skLineSegment(sketch, "E585", {"start": v(-237.26, 138.75) * mm, "end": v(-241.76, 139.61) * mm});
            skLineSegment(sketch, "E586", {"start": v(-241.76, 139.61) * mm, "end": v(-245.84, 141.06) * mm});
            skLineSegment(sketch, "E587", {"start": v(-245.84, 141.06) * mm, "end": v(-249.5, 143.1) * mm});
            skLineSegment(sketch, "E588", {"start": v(-249.5, 143.1) * mm, "end": v(-252.77, 145.78) * mm});
            skLineSegment(sketch, "E589", {"start": v(-252.77, 145.78) * mm, "end": v(-255.11, 148.86) * mm});
            skLineSegment(sketch, "E590", {"start": v(-255.11, 148.86) * mm, "end": v(-256.54, 152.36) * mm});
            skLineSegment(sketch, "E591", {"start": v(-256.54, 152.36) * mm, "end": v(-257.05, 156.25) * mm});
            skLineSegment(sketch, "E592", {"start": v(-257.05, 156.25) * mm, "end": v(-256.63, 160.18) * mm});
            skLineSegment(sketch, "E593", {"start": v(-256.63, 160.18) * mm, "end": v(-255.3, 163.7) * mm});
            skLineSegment(sketch, "E594", {"start": v(-255.3, 163.7) * mm, "end": v(-253.04, 166.8) * mm});
            skLineSegment(sketch, "E595", {"start": v(-253.04, 166.8) * mm, "end": v(-249.85, 169.48) * mm});
            skLineSegment(sketch, "E596", {"start": v(-249.85, 169.48) * mm, "end": v(-246.24, 171.5) * mm});
            skLineSegment(sketch, "E597", {"start": v(-246.24, 171.5) * mm, "end": v(-242.2, 172.95) * mm});
            skLineSegment(sketch, "E598", {"start": v(-242.2, 172.95) * mm, "end": v(-237.74, 173.82) * mm});
            skLineSegment(sketch, "E599", {"start": v(-237.74, 173.82) * mm, "end": v(-232.85, 174.11) * mm});
            skLineSegment(sketch, "E600", {"start": v(-232.85, 174.11) * mm, "end": v(-178.14, 174.13) * mm});
            skLineSegment(sketch, "E601", {"start": v(-92.9, 151.85) * mm, "end": v(-93.36, 147.03) * mm});
            skLineSegment(sketch, "E602", {"start": v(-93.36, 147.03) * mm, "end": v(-94.92, 142.7) * mm});
            skLineSegment(sketch, "E603", {"start": v(-94.92, 142.7) * mm, "end": v(-97.6, 138.83) * mm});
            skLineSegment(sketch, "E604", {"start": v(-97.6, 138.83) * mm, "end": v(-101.38, 135.44) * mm});
            skLineSegment(sketch, "E605", {"start": v(-101.38, 135.44) * mm, "end": v(-105.81, 132.83) * mm});
            skLineSegment(sketch, "E606", {"start": v(-105.81, 132.83) * mm, "end": v(-110.76, 130.96) * mm});
            skLineSegment(sketch, "E607", {"start": v(-110.76, 130.96) * mm, "end": v(-116.23, 129.84) * mm});
            skLineSegment(sketch, "E608", {"start": v(-116.23, 129.84) * mm, "end": v(-122.22, 129.47) * mm});
            skLineSegment(sketch, "E609", {"start": v(-122.22, 129.47) * mm, "end": v(-153.83, 129.46) * mm});
            skLineSegment(sketch, "E610", {"start": v(-153.83, 129.46) * mm, "end": v(-153.57, 114.43) * mm});
            skLineSegment(sketch, "E611", {"start": v(-153.57, 114.43) * mm, "end": v(-172.29, 114.42) * mm});
            skLineSegment(sketch, "E612", {"start": v(-172.29, 114.42) * mm, "end": v(-172.78, 144.95) * mm});
            skLineSegment(sketch, "E613", {"start": v(-172.78, 144.95) * mm, "end": v(-120.68, 144.96) * mm});
            skLineSegment(sketch, "E614", {"start": v(-120.68, 144.96) * mm, "end": v(-117.14, 145.44) * mm});
            skLineSegment(sketch, "E615", {"start": v(-117.14, 145.44) * mm, "end": v(-114.22, 146.87) * mm});
            skLineSegment(sketch, "E616", {"start": v(-114.22, 146.87) * mm, "end": v(-112.28, 149.09) * mm});
            skLineSegment(sketch, "E617", {"start": v(-112.28, 149.09) * mm, "end": v(-111.68, 151.92) * mm});
            skLineSegment(sketch, "E618", {"start": v(-111.68, 151.92) * mm, "end": v(-112.4, 154.73) * mm});
            skLineSegment(sketch, "E619", {"start": v(-112.4, 154.73) * mm, "end": v(-114.41, 156.88) * mm});
            skLineSegment(sketch, "E620", {"start": v(-114.41, 156.88) * mm, "end": v(-117.38, 158.25) * mm});
            skLineSegment(sketch, "E621", {"start": v(-117.38, 158.25) * mm, "end": v(-120.93, 158.7) * mm});
            skLineSegment(sketch, "E622", {"start": v(-120.93, 158.7) * mm, "end": v(-173, 158.68) * mm});
            skLineSegment(sketch, "E623", {"start": v(-173, 158.68) * mm, "end": v(-160.88, 174.14) * mm});
            skLineSegment(sketch, "E624", {"start": v(-160.88, 174.14) * mm, "end": v(-122.97, 174.16) * mm});
            skLineSegment(sketch, "E625", {"start": v(-122.97, 174.16) * mm, "end": v(-117.02, 173.79) * mm});
            skLineSegment(sketch, "E626", {"start": v(-117.02, 173.79) * mm, "end": v(-111.54, 172.67) * mm});
            skLineSegment(sketch, "E627", {"start": v(-111.54, 172.67) * mm, "end": v(-106.54, 170.82) * mm});
            skLineSegment(sketch, "E628", {"start": v(-106.54, 170.82) * mm, "end": v(-102.02, 168.22) * mm});
            skLineSegment(sketch, "E629", {"start": v(-102.02, 168.22) * mm, "end": v(-98.1, 164.84) * mm});
            skLineSegment(sketch, "E630", {"start": v(-98.1, 164.84) * mm, "end": v(-95.28, 160.99) * mm});
            skLineSegment(sketch, "E631", {"start": v(-95.28, 160.99) * mm, "end": v(-93.55, 156.65) * mm});
            skLineSegment(sketch, "E632", {"start": v(-93.55, 156.65) * mm, "end": v(-92.9, 151.85) * mm});
            skLineSegment(sketch, "E633", {"start": v(1.11, 144.92) * mm, "end": v(0.62, 138.65) * mm});
            skLineSegment(sketch, "E634", {"start": v(0.62, 138.65) * mm, "end": v(-1.19, 132.93) * mm});
            skLineSegment(sketch, "E635", {"start": v(-1.19, 132.93) * mm, "end": v(-4.3, 127.76) * mm});
            skLineSegment(sketch, "E636", {"start": v(-4.3, 127.76) * mm, "end": v(-8.72, 123.15) * mm});
            skLineSegment(sketch, "E637", {"start": v(-8.72, 123.15) * mm, "end": v(-14.15, 119.35) * mm});
            skLineSegment(sketch, "E638", {"start": v(-14.15, 119.35) * mm, "end": v(-20.29, 116.64) * mm});
            skLineSegment(sketch, "E639", {"start": v(-20.29, 116.64) * mm, "end": v(-27.12, 115) * mm});
            skLineSegment(sketch, "E640", {"start": v(-27.12, 115) * mm, "end": v(-34.66, 114.46) * mm});
            skLineSegment(sketch, "E641", {"start": v(-34.66, 114.46) * mm, "end": v(-52.87, 114.46) * mm});
            skLineSegment(sketch, "E642", {"start": v(-52.87, 114.46) * mm, "end": v(-60.47, 115) * mm});
            skLineSegment(sketch, "E643", {"start": v(-60.47, 115) * mm, "end": v(-67.4, 116.62) * mm});
            skLineSegment(sketch, "E644", {"start": v(-67.4, 116.62) * mm, "end": v(-73.67, 119.33) * mm});
            skLineSegment(sketch, "E645", {"start": v(-73.67, 119.33) * mm, "end": v(-79.27, 123.13) * mm});
            skLineSegment(sketch, "E646", {"start": v(-79.27, 123.13) * mm, "end": v(-83.9, 127.74) * mm});
            skLineSegment(sketch, "E647", {"start": v(-83.9, 127.74) * mm, "end": v(-87.24, 132.9) * mm});
            skLineSegment(sketch, "E648", {"start": v(-87.24, 132.9) * mm, "end": v(-89.3, 138.62) * mm});
            skLineSegment(sketch, "E649", {"start": v(-89.3, 138.62) * mm, "end": v(-90.06, 144.89) * mm});
            skLineSegment(sketch, "E650", {"start": v(-90.06, 144.89) * mm, "end": v(-89.55, 151.12) * mm});
            skLineSegment(sketch, "E651", {"start": v(-89.55, 151.12) * mm, "end": v(-87.74, 156.73) * mm});
            skLineSegment(sketch, "E652", {"start": v(-87.74, 156.73) * mm, "end": v(-84.63, 161.71) * mm});
            skLineSegment(sketch, "E653", {"start": v(-84.63, 161.71) * mm, "end": v(-80.24, 166.07) * mm});
            skLineSegment(sketch, "E654", {"start": v(-80.24, 166.07) * mm, "end": v(-74.82, 169.62) * mm});
            skLineSegment(sketch, "E655", {"start": v(-74.82, 169.62) * mm, "end": v(-68.68, 172.15) * mm});
            skLineSegment(sketch, "E656", {"start": v(-68.68, 172.15) * mm, "end": v(-61.8, 173.67) * mm});
            skLineSegment(sketch, "E657", {"start": v(-61.8, 173.67) * mm, "end": v(-54.17, 174.18) * mm});
            skLineSegment(sketch, "E658", {"start": v(-54.17, 174.18) * mm, "end": v(-36, 174.19) * mm});
            skLineSegment(sketch, "E659", {"start": v(-36, 174.19) * mm, "end": v(-28.36, 173.69) * mm});
            skLineSegment(sketch, "E660", {"start": v(-28.36, 173.69) * mm, "end": v(-21.42, 172.17) * mm});
            skLineSegment(sketch, "E661", {"start": v(-21.42, 172.17) * mm, "end": v(-15.17, 169.64) * mm});
            skLineSegment(sketch, "E662", {"start": v(-15.17, 169.64) * mm, "end": v(-9.62, 166.1) * mm});
            skLineSegment(sketch, "E663", {"start": v(-9.62, 166.1) * mm, "end": v(-5.04, 161.74) * mm});
            skLineSegment(sketch, "E664", {"start": v(-5.04, 161.74) * mm, "end": v(-1.73, 156.76) * mm});
            skLineSegment(sketch, "E665", {"start": v(-1.73, 156.76) * mm, "end": v(0.32, 151.15) * mm});
            skLineSegment(sketch, "E666", {"start": v(0.32, 151.15) * mm, "end": v(1.11, 144.92) * mm});
            skLineSegment(sketch, "E667", {"start": v(-35.66, 158.73) * mm, "end": v(-53.83, 158.73) * mm});
            skLineSegment(sketch, "E668", {"start": v(-53.83, 158.73) * mm, "end": v(-57.54, 158.47) * mm});
            skLineSegment(sketch, "E669", {"start": v(-57.54, 158.47) * mm, "end": v(-60.9, 157.7) * mm});
            skLineSegment(sketch, "E670", {"start": v(-60.9, 157.7) * mm, "end": v(-63.9, 156.42) * mm});
            skLineSegment(sketch, "E671", {"start": v(-63.9, 156.42) * mm, "end": v(-66.55, 154.63) * mm});
            skLineSegment(sketch, "E672", {"start": v(-66.55, 154.63) * mm, "end": v(-68.7, 152.43) * mm});
            skLineSegment(sketch, "E673", {"start": v(-68.7, 152.43) * mm, "end": v(-70.22, 149.96) * mm});
            skLineSegment(sketch, "E674", {"start": v(-70.22, 149.96) * mm, "end": v(-71.1, 147.2) * mm});
            skLineSegment(sketch, "E675", {"start": v(-71.1, 147.2) * mm, "end": v(-71.35, 144.15) * mm});
            skLineSegment(sketch, "E676", {"start": v(-71.35, 144.15) * mm, "end": v(-70.97, 141.11) * mm});
            skLineSegment(sketch, "E677", {"start": v(-70.97, 141.11) * mm, "end": v(-69.97, 138.38) * mm});
            skLineSegment(sketch, "E678", {"start": v(-69.97, 138.38) * mm, "end": v(-68.35, 135.95) * mm});
            skLineSegment(sketch, "E679", {"start": v(-68.35, 135.95) * mm, "end": v(-66.1, 133.83) * mm});
            skLineSegment(sketch, "E680", {"start": v(-66.1, 133.83) * mm, "end": v(-63.38, 132.1) * mm});
            skLineSegment(sketch, "E681", {"start": v(-63.38, 132.1) * mm, "end": v(-60.33, 130.88) * mm});
            skLineSegment(sketch, "E682", {"start": v(-60.33, 130.88) * mm, "end": v(-56.93, 130.14) * mm});
            skLineSegment(sketch, "E683", {"start": v(-56.93, 130.14) * mm, "end": v(-53.2, 129.9) * mm});
            skLineSegment(sketch, "E684", {"start": v(-53.2, 129.9) * mm, "end": v(-35.01, 129.9) * mm});
            skLineSegment(sketch, "E685", {"start": v(-35.01, 129.9) * mm, "end": v(-31.3, 130.15) * mm});
            skLineSegment(sketch, "E686", {"start": v(-31.3, 130.15) * mm, "end": v(-27.93, 130.89) * mm});
            skLineSegment(sketch, "E687", {"start": v(-27.93, 130.89) * mm, "end": v(-24.93, 132.12) * mm});
            skLineSegment(sketch, "E688", {"start": v(-24.93, 132.12) * mm, "end": v(-22.28, 133.84) * mm});
            skLineSegment(sketch, "E689", {"start": v(-22.28, 133.84) * mm, "end": v(-20.13, 135.97) * mm});
            skLineSegment(sketch, "E690", {"start": v(-20.13, 135.97) * mm, "end": v(-18.62, 138.4) * mm});
            skLineSegment(sketch, "E691", {"start": v(-18.62, 138.4) * mm, "end": v(-17.74, 141.13) * mm});
            skLineSegment(sketch, "E692", {"start": v(-17.74, 141.13) * mm, "end": v(-17.5, 144.17) * mm});
            skLineSegment(sketch, "E693", {"start": v(-17.5, 144.17) * mm, "end": v(-17.88, 147.21) * mm});
            skLineSegment(sketch, "E694", {"start": v(-17.88, 147.21) * mm, "end": v(-18.9, 149.97) * mm});
            skLineSegment(sketch, "E695", {"start": v(-18.9, 149.97) * mm, "end": v(-20.54, 152.45) * mm});
            skLineSegment(sketch, "E696", {"start": v(-20.54, 152.45) * mm, "end": v(-22.8, 154.64) * mm});
            skLineSegment(sketch, "E697", {"start": v(-22.8, 154.64) * mm, "end": v(-25.54, 156.43) * mm});
            skLineSegment(sketch, "E698", {"start": v(-25.54, 156.43) * mm, "end": v(-28.6, 157.71) * mm});
            skLineSegment(sketch, "E699", {"start": v(-28.6, 157.71) * mm, "end": v(-31.97, 158.48) * mm});
            skLineSegment(sketch, "E700", {"start": v(-31.97, 158.48) * mm, "end": v(-35.66, 158.73) * mm});
            skLineSegment(sketch, "E701", {"start": v(97.07, 114.5) * mm, "end": v(69.78, 114.49) * mm});
            skLineSegment(sketch, "E702", {"start": v(69.78, 114.49) * mm, "end": v(51.08, 129.52) * mm});
            skLineSegment(sketch, "E703", {"start": v(51.08, 129.52) * mm, "end": v(25.24, 129.51) * mm});
            skLineSegment(sketch, "E704", {"start": v(25.24, 129.51) * mm, "end": v(25.62, 114.48) * mm});
            skLineSegment(sketch, "E705", {"start": v(25.62, 114.48) * mm, "end": v(6.8, 114.47) * mm});
            skLineSegment(sketch, "E706", {"start": v(6.8, 114.47) * mm, "end": v(6.06, 145) * mm});
            skLineSegment(sketch, "E707", {"start": v(6.06, 145) * mm, "end": v(58.22, 145.02) * mm});
            skLineSegment(sketch, "E708", {"start": v(58.22, 145.02) * mm, "end": v(62.57, 145.38) * mm});
            skLineSegment(sketch, "E709", {"start": v(62.57, 145.38) * mm, "end": v(66.07, 146.44) * mm});
            skLineSegment(sketch, "E710", {"start": v(66.07, 146.44) * mm, "end": v(67.76, 147.46) * mm});
            skLineSegment(sketch, "E711", {"start": v(67.76, 147.46) * mm, "end": v(68.96, 148.7) * mm});
            skLineSegment(sketch, "E712", {"start": v(68.96, 148.7) * mm, "end": v(69.66, 150.15) * mm});
            skLineSegment(sketch, "E713", {"start": v(69.66, 150.15) * mm, "end": v(69.86, 151.82) * mm});
            skLineSegment(sketch, "E714", {"start": v(69.86, 151.82) * mm, "end": v(69.04, 154.86) * mm});
            skLineSegment(sketch, "E715", {"start": v(69.04, 154.86) * mm, "end": v(66.76, 157.03) * mm});
            skLineSegment(sketch, "E716", {"start": v(66.76, 157.03) * mm, "end": v(63.03, 158.33) * mm});
            skLineSegment(sketch, "E717", {"start": v(63.03, 158.33) * mm, "end": v(57.85, 158.77) * mm});
            skLineSegment(sketch, "E718", {"start": v(57.85, 158.77) * mm, "end": v(5.73, 158.75) * mm});
            skLineSegment(sketch, "E719", {"start": v(5.73, 158.75) * mm, "end": v(17.57, 174.21) * mm});
            skLineSegment(sketch, "E720", {"start": v(17.57, 174.21) * mm, "end": v(55.67, 174.23) * mm});
            skLineSegment(sketch, "E721", {"start": v(55.67, 174.23) * mm, "end": v(62.42, 173.9) * mm});
            skLineSegment(sketch, "E722", {"start": v(62.42, 173.9) * mm, "end": v(68.52, 172.9) * mm});
            skLineSegment(sketch, "E723", {"start": v(68.52, 172.9) * mm, "end": v(73.97, 171.26) * mm});
            skLineSegment(sketch, "E724", {"start": v(73.97, 171.26) * mm, "end": v(78.77, 168.94) * mm});
            skLineSegment(sketch, "E725", {"start": v(78.77, 168.94) * mm, "end": v(83.19, 165.6) * mm});
            skLineSegment(sketch, "E726", {"start": v(83.19, 165.6) * mm, "end": v(86.39, 161.63) * mm});
            skLineSegment(sketch, "E727", {"start": v(86.39, 161.63) * mm, "end": v(88.37, 157) * mm});
            skLineSegment(sketch, "E728", {"start": v(88.37, 157) * mm, "end": v(89.14, 151.74) * mm});
            skLineSegment(sketch, "E729", {"start": v(89.14, 151.74) * mm, "end": v(88.98, 148.67) * mm});
            skLineSegment(sketch, "E730", {"start": v(88.98, 148.67) * mm, "end": v(88.31, 145.74) * mm});
            skLineSegment(sketch, "E731", {"start": v(88.31, 145.74) * mm, "end": v(87.15, 142.97) * mm});
            skLineSegment(sketch, "E732", {"start": v(87.15, 142.97) * mm, "end": v(85.48, 140.35) * mm});
            skLineSegment(sketch, "E733", {"start": v(85.48, 140.35) * mm, "end": v(83.36, 137.94) * mm});
            skLineSegment(sketch, "E734", {"start": v(83.36, 137.94) * mm, "end": v(80.85, 135.84) * mm});
            skLineSegment(sketch, "E735", {"start": v(80.85, 135.84) * mm, "end": v(74.65, 132.5) * mm});
            skLineSegment(sketch, "E736", {"start": v(74.65, 132.5) * mm, "end": v(97.07, 114.5) * mm});
            skLineSegment(sketch, "E737", {"start": v(170.64, 174.27) * mm, "end": v(158.98, 158.8) * mm});
            skLineSegment(sketch, "E738", {"start": v(158.98, 158.8) * mm, "end": v(140.87, 158.8) * mm});
            skLineSegment(sketch, "E739", {"start": v(140.87, 158.8) * mm, "end": v(142.23, 114.5) * mm});
            skLineSegment(sketch, "E740", {"start": v(142.23, 114.5) * mm, "end": v(123.4, 114.5) * mm});
            skLineSegment(sketch, "E741", {"start": v(123.4, 114.5) * mm, "end": v(122.09, 158.8) * mm});
            skLineSegment(sketch, "E742", {"start": v(122.09, 158.8) * mm, "end": v(97.2, 158.78) * mm});
            skLineSegment(sketch, "E743", {"start": v(97.2, 158.78) * mm, "end": v(108.82, 174.25) * mm});
            skLineSegment(sketch, "E744", {"start": v(108.82, 174.25) * mm, "end": v(170.64, 174.27) * mm});
            skLineSegment(sketch, "E745", {"start": v(251.2, 174.3) * mm, "end": v(239.67, 158.83) * mm});
            skLineSegment(sketch, "E746", {"start": v(239.67, 158.83) * mm, "end": v(196.9, 158.82) * mm});
            skLineSegment(sketch, "E747", {"start": v(196.9, 158.82) * mm, "end": v(194.35, 158.22) * mm});
            skLineSegment(sketch, "E748", {"start": v(194.35, 158.22) * mm, "end": v(193.73, 157.46) * mm});
            skLineSegment(sketch, "E749", {"start": v(193.73, 157.46) * mm, "end": v(193.55, 156.41) * mm});
            skLineSegment(sketch, "E750", {"start": v(193.55, 156.41) * mm, "end": v(193.8, 155.36) * mm});
            skLineSegment(sketch, "E751", {"start": v(193.8, 155.36) * mm, "end": v(194.47, 154.6) * mm});
            skLineSegment(sketch, "E752", {"start": v(194.47, 154.6) * mm, "end": v(197.07, 154) * mm});
            skLineSegment(sketch, "E753", {"start": v(197.07, 154) * mm, "end": v(227.86, 154.02) * mm});
            skLineSegment(sketch, "E754", {"start": v(227.86, 154.02) * mm, "end": v(233.14, 153.69) * mm});
            skLineSegment(sketch, "E755", {"start": v(233.14, 153.69) * mm, "end": v(238, 152.7) * mm});
            skLineSegment(sketch, "E756", {"start": v(238, 152.7) * mm, "end": v(242.42, 151.04) * mm});
            skLineSegment(sketch, "E757", {"start": v(242.42, 151.04) * mm, "end": v(246.42, 148.72) * mm});
            skLineSegment(sketch, "E758", {"start": v(246.42, 148.72) * mm, "end": v(249.87, 145.7) * mm});
            skLineSegment(sketch, "E759", {"start": v(249.87, 145.7) * mm, "end": v(252.38, 142.26) * mm});
            skLineSegment(sketch, "E760", {"start": v(252.38, 142.26) * mm, "end": v(253.95, 138.4) * mm});
            skLineSegment(sketch, "E761", {"start": v(253.95, 138.4) * mm, "end": v(254.58, 134.14) * mm});
            skLineSegment(sketch, "E762", {"start": v(254.58, 134.14) * mm, "end": v(254.25, 129.91) * mm});
            skLineSegment(sketch, "E763", {"start": v(254.25, 129.91) * mm, "end": v(252.94, 126.1) * mm});
            skLineSegment(sketch, "E764", {"start": v(252.94, 126.1) * mm, "end": v(250.65, 122.73) * mm});
            skLineSegment(sketch, "E765", {"start": v(250.65, 122.73) * mm, "end": v(247.37, 119.77) * mm});
            skLineSegment(sketch, "E766", {"start": v(247.37, 119.77) * mm, "end": v(243.6, 117.48) * mm});
            skLineSegment(sketch, "E767", {"start": v(243.6, 117.48) * mm, "end": v(239.33, 115.85) * mm});
            skLineSegment(sketch, "E768", {"start": v(239.33, 115.85) * mm, "end": v(234.55, 114.86) * mm});
            skLineSegment(sketch, "E769", {"start": v(234.55, 114.86) * mm, "end": v(229.26, 114.53) * mm});
            skLineSegment(sketch, "E770", {"start": v(229.26, 114.53) * mm, "end": v(173.85, 114.52) * mm});
            skLineSegment(sketch, "E771", {"start": v(173.85, 114.52) * mm, "end": v(185.43, 129.97) * mm});
            skLineSegment(sketch, "E772", {"start": v(185.43, 129.97) * mm, "end": v(228.71, 129.98) * mm});
            skLineSegment(sketch, "E773", {"start": v(228.71, 129.98) * mm, "end": v(231.5, 130.23) * mm});
            skLineSegment(sketch, "E774", {"start": v(231.5, 130.23) * mm, "end": v(233.96, 130.98) * mm});
            skLineSegment(sketch, "E775", {"start": v(233.96, 130.98) * mm, "end": v(236.18, 132.45) * mm});
            skLineSegment(sketch, "E776", {"start": v(236.18, 132.45) * mm, "end": v(236.86, 134.38) * mm});
            skLineSegment(sketch, "E777", {"start": v(236.86, 134.38) * mm, "end": v(236.04, 136.35) * mm});
            skLineSegment(sketch, "E778", {"start": v(236.04, 136.35) * mm, "end": v(233.72, 137.78) * mm});
            skLineSegment(sketch, "E779", {"start": v(233.72, 137.78) * mm, "end": v(231.25, 138.4) * mm});
            skLineSegment(sketch, "E780", {"start": v(231.25, 138.4) * mm, "end": v(228.4, 138.6) * mm});
            skLineSegment(sketch, "E781", {"start": v(228.4, 138.6) * mm, "end": v(197.6, 138.6) * mm});
            skLineSegment(sketch, "E782", {"start": v(197.6, 138.6) * mm, "end": v(192.67, 138.89) * mm});
            skLineSegment(sketch, "E783", {"start": v(192.67, 138.89) * mm, "end": v(188.15, 139.75) * mm});
            skLineSegment(sketch, "E784", {"start": v(188.15, 139.75) * mm, "end": v(184.03, 141.2) * mm});
            skLineSegment(sketch, "E785", {"start": v(184.03, 141.2) * mm, "end": v(180.32, 143.23) * mm});
            skLineSegment(sketch, "E786", {"start": v(180.32, 143.23) * mm, "end": v(177, 145.92) * mm});
            skLineSegment(sketch, "E787", {"start": v(177, 145.92) * mm, "end": v(174.6, 149.01) * mm});
            skLineSegment(sketch, "E788", {"start": v(174.6, 149.01) * mm, "end": v(173.1, 152.5) * mm});
            skLineSegment(sketch, "E789", {"start": v(173.1, 152.5) * mm, "end": v(172.5, 156.4) * mm});
            skLineSegment(sketch, "E790", {"start": v(172.5, 156.4) * mm, "end": v(172.84, 160.34) * mm});
            skLineSegment(sketch, "E791", {"start": v(172.84, 160.34) * mm, "end": v(174.11, 163.85) * mm});
            skLineSegment(sketch, "E792", {"start": v(174.11, 163.85) * mm, "end": v(176.32, 166.96) * mm});
            skLineSegment(sketch, "E793", {"start": v(176.32, 166.96) * mm, "end": v(179.46, 169.64) * mm});
            skLineSegment(sketch, "E794", {"start": v(179.46, 169.64) * mm, "end": v(183.04, 171.67) * mm});
            skLineSegment(sketch, "E795", {"start": v(183.04, 171.67) * mm, "end": v(187.05, 173.12) * mm});
            skLineSegment(sketch, "E796", {"start": v(187.05, 173.12) * mm, "end": v(191.5, 174) * mm});
            skLineSegment(sketch, "E797", {"start": v(191.5, 174) * mm, "end": v(196.4, 174.28) * mm});
            skLineSegment(sketch, "E798", {"start": v(196.4, 174.28) * mm, "end": v(251.2, 174.3) * mm});
            skLineSegment(sketch, "E799", {"start": v(-1025.53, 4.74) * mm, "end": v(-1007.15, 4.15) * mm});
            skLineSegment(sketch, "E800", {"start": v(-1026.67, -45.2) * mm, "end": v(-1025.53, 4.74) * mm});
            skLineSegment(sketch, "E801", {"start": v(-913.84, 81.87) * mm, "end": v(-900.2, 82.85) * mm});
            skLineSegment(sketch, "E802", {"start": v(-900.2, 82.85) * mm, "end": v(-891.2, 85.76) * mm});
            skLineSegment(sketch, "E803", {"start": v(-898.8, 122.7) * mm, "end": v(-912.2, 123.86) * mm});
            skLineSegment(sketch, "E804", {"start": v(-881.85, 105.13) * mm, "end": v(-883.64, 113.33) * mm});
            skLineSegment(sketch, "E805", {"start": v(-923.01, 123.86) * mm, "end": v(-923.77, 81.87) * mm});
            skLineSegment(sketch, "E806", {"start": v(-905.44, -45.2) * mm, "end": v(-1026.67, -45.2) * mm});
            skLineSegment(sketch, "E807", {"start": v(-882.55, 99.47) * mm, "end": v(-881.85, 105.13) * mm});
            skLineSegment(sketch, "E808", {"start": v(-904.6, 4.16) * mm, "end": v(-905.44, -45.2) * mm});
            skLineSegment(sketch, "E809", {"start": v(-889.29, 119.19) * mm, "end": v(-898.8, 122.7) * mm});
            skLineSegment(sketch, "E810", {"start": v(-923.77, 81.87) * mm, "end": v(-913.84, 81.87) * mm});
            skLineSegment(sketch, "E811", {"start": v(-885.7, 91.13) * mm, "end": v(-882.55, 99.47) * mm});
            skLineSegment(sketch, "E812", {"start": v(-891.2, 85.76) * mm, "end": v(-885.7, 91.13) * mm});
            skLineSegment(sketch, "E813", {"start": v(-925.17, 4.75) * mm, "end": v(-904.6, 4.16) * mm});
            skLineSegment(sketch, "E814", {"start": v(-883.64, 113.33) * mm, "end": v(-889.29, 119.19) * mm});
            skLineSegment(sketch, "E815", {"start": v(-811.59, 141.92) * mm, "end": v(-804.6, 131) * mm});
            skLineSegment(sketch, "E816", {"start": v(-905.65, 169.15) * mm, "end": v(-884.39, 169.16) * mm});
            skLineSegment(sketch, "E817", {"start": v(-833.82, 159.22) * mm, "end": v(-821.43, 151.47) * mm});
            skLineSegment(sketch, "E818", {"start": v(-801.24, 88.94) * mm, "end": v(-809.56, 69.57) * mm});
            skLineSegment(sketch, "E819", {"start": v(-809.56, 69.57) * mm, "end": v(-823.72, 54.26) * mm});
            skLineSegment(sketch, "E820", {"start": v(-804.6, 131) * mm, "end": v(-800.48, 118.68) * mm});
            skLineSegment(sketch, "E821", {"start": v(-865.3, 168.06) * mm, "end": v(-848.44, 164.75) * mm});
            skLineSegment(sketch, "E822", {"start": v(-800.48, 118.68) * mm, "end": v(-799.23, 104.98) * mm});
            skLineSegment(sketch, "E823", {"start": v(-875.32, 37.84) * mm, "end": v(-880.76, 37.69) * mm});
            skLineSegment(sketch, "E824", {"start": v(-1021.78, 169.54) * mm, "end": v(-905.65, 169.15) * mm});
            skLineSegment(sketch, "E825", {"start": v(-848.44, 164.75) * mm, "end": v(-833.82, 159.22) * mm});
            skLineSegment(sketch, "E826", {"start": v(-880.76, 37.69) * mm, "end": v(-924.58, 37.68) * mm});
            skLineSegment(sketch, "E827", {"start": v(-924.58, 37.68) * mm, "end": v(-925.17, 4.75) * mm});
            skLineSegment(sketch, "E828", {"start": v(-1004.6, 120.78) * mm, "end": v(-1022.9, 120.2) * mm});
            skLineSegment(sketch, "E829", {"start": v(-884.39, 169.16) * mm, "end": v(-865.3, 168.06) * mm});
            skLineSegment(sketch, "E830", {"start": v(-821.43, 151.47) * mm, "end": v(-811.59, 141.92) * mm});
            skLineSegment(sketch, "E831", {"start": v(-799.23, 104.98) * mm, "end": v(-801.24, 88.94) * mm});
            skLineSegment(sketch, "E832", {"start": v(-1007.15, 4.15) * mm, "end": v(-1004.6, 120.78) * mm});
            skLineSegment(sketch, "E833", {"start": v(-843.5, 43.63) * mm, "end": v(-868.67, 38.28) * mm});
            skLineSegment(sketch, "E834", {"start": v(-823.72, 54.26) * mm, "end": v(-843.5, 43.63) * mm});
            skLineSegment(sketch, "E835", {"start": v(-868.67, 38.28) * mm, "end": v(-875.32, 37.84) * mm});
            skLineSegment(sketch, "E836", {"start": v(-1022.9, 120.2) * mm, "end": v(-1021.78, 169.54) * mm});
            skLineSegment(sketch, "E837", {"start": v(-573.8, 76.64) * mm, "end": v(-583.92, 64.24) * mm});
            skLineSegment(sketch, "E838", {"start": v(-578.25, 145.11) * mm, "end": v(-571.05, 134.7) * mm});
            skLineSegment(sketch, "E839", {"start": v(-635.07, 168.71) * mm, "end": v(-616.8, 165.75) * mm});
            skLineSegment(sketch, "E840", {"start": v(-565.32, 108.85) * mm, "end": v(-567.45, 91.86) * mm});
            skLineSegment(sketch, "E841", {"start": v(-633.28, -45.2) * mm, "end": v(-671.7, 42.55) * mm});
            skLineSegment(sketch, "E842", {"start": v(-671.7, 42.55) * mm, "end": v(-693.96, 42.54) * mm});
            skLineSegment(sketch, "E843", {"start": v(-693.96, 42.54) * mm, "end": v(-694.25, 4.77) * mm});
            skLineSegment(sketch, "E844", {"start": v(-694.25, 4.77) * mm, "end": v(-677.26, 4.19) * mm});
            skLineSegment(sketch, "E845", {"start": v(-656.04, 169.7) * mm, "end": v(-635.07, 168.71) * mm});
            skLineSegment(sketch, "E846", {"start": v(-601.22, 160.8) * mm, "end": v(-588.34, 153.87) * mm});
            skLineSegment(sketch, "E847", {"start": v(-588.34, 153.87) * mm, "end": v(-578.25, 145.11) * mm});
            skLineSegment(sketch, "E848", {"start": v(-567.45, 91.86) * mm, "end": v(-573.8, 76.64) * mm});
            skLineSegment(sketch, "E849", {"start": v(-571.05, 134.7) * mm, "end": v(-566.74, 122.6) * mm});
            skLineSegment(sketch, "E850", {"start": v(-583.92, 64.24) * mm, "end": v(-597.36, 55.7) * mm});
            skLineSegment(sketch, "E851", {"start": v(-597.36, 55.7) * mm, "end": v(-566.4, 4.2) * mm});
            skLineSegment(sketch, "E852", {"start": v(-566.43, 3.62) * mm, "end": v(-551.63, 3.62) * mm});
            skLineSegment(sketch, "E853", {"start": v(-566.74, 122.6) * mm, "end": v(-565.32, 108.85) * mm});
            skLineSegment(sketch, "E854", {"start": v(-616.8, 165.75) * mm, "end": v(-601.22, 160.8) * mm});
            skLineSegment(sketch, "E855", {"start": v(-793.88, 120.42) * mm, "end": v(-793.28, 169.64) * mm});
            skLineSegment(sketch, "E856", {"start": v(-776.89, 4.18) * mm, "end": v(-775.56, 121) * mm});
            skLineSegment(sketch, "E857", {"start": v(-795.9, -45.2) * mm, "end": v(-795.3, 4.76) * mm});
            skLineSegment(sketch, "E858", {"start": v(-795.3, 4.76) * mm, "end": v(-776.89, 4.18) * mm});
            skLineSegment(sketch, "E859", {"start": v(-775.56, 121) * mm, "end": v(-793.88, 120.42) * mm});
            skLineSegment(sketch, "E860", {"start": v(-677.6, -45.2) * mm, "end": v(-795.9, -45.2) * mm});
            skLineSegment(sketch, "E861", {"start": v(-677.26, 4.19) * mm, "end": v(-677.6, -45.2) * mm});
            skLineSegment(sketch, "E862", {"start": v(-88.74, -67.5) * mm, "end": v(-81.51, -61.93) * mm});
            skLineSegment(sketch, "E863", {"start": v(-81.51, -61.93) * mm, "end": v(-80.77, -61.36) * mm});
            skLineSegment(sketch, "E864", {"start": v(-80.7, -65.17) * mm, "end": v(-81.75, -66.3) * mm});
            skLineSegment(sketch, "E865", {"start": v(-81.75, -66.3) * mm, "end": v(-87.9, -72.85) * mm});
            skLineSegment(sketch, "E866", {"start": v(-43.08, -67.76) * mm, "end": v(-34.6, -61.35) * mm});
            skLineSegment(sketch, "E867", {"start": v(-34.6, -61.35) * mm, "end": v(-34.12, -60.99) * mm});
            skLineSegment(sketch, "E868", {"start": v(-34.02, -65.3) * mm, "end": v(-34.72, -65.95) * mm});
            skLineSegment(sketch, "E869", {"start": v(-34.72, -65.95) * mm, "end": v(-47.4, -77.92) * mm});
            skLineSegment(sketch, "E870", {"start": v(-81.36, -70.13) * mm, "end": v(-81.75, -66.3) * mm});
            skLineSegment(sketch, "E871", {"start": v(-81.75, -66.3) * mm, "end": v(-81.89, -64.92) * mm});
            skLineSegment(sketch, "E872", {"start": v(-81.89, -64.92) * mm, "end": v(-81.51, -61.93) * mm});
            skLineSegment(sketch, "E873", {"start": v(-81.51, -61.93) * mm, "end": v(-81.21, -59.55) * mm});
            skLineSegment(sketch, "E874", {"start": v(15.42, -65.42) * mm, "end": v(14.55, -66.15) * mm});
            skLineSegment(sketch, "E875", {"start": v(14.55, -66.15) * mm, "end": v(-4.98, -82.48) * mm});
            skLineSegment(sketch, "E876", {"start": v(-34.27, -68.97) * mm, "end": v(-34.72, -65.95) * mm});
            skLineSegment(sketch, "E877", {"start": v(-34.72, -65.95) * mm, "end": v(-35.06, -63.67) * mm});
            skLineSegment(sketch, "E878", {"start": v(-35.06, -63.67) * mm, "end": v(-34.6, -61.35) * mm});
            skLineSegment(sketch, "E879", {"start": v(-34.6, -61.35) * mm, "end": v(-34.02, -58.43) * mm});
            skLineSegment(sketch, "E880", {"start": v(0.42, -72.36) * mm, "end": v(14.56, -61.93) * mm});
            skLineSegment(sketch, "E881", {"start": v(14.56, -61.93) * mm, "end": v(15.32, -61.37) * mm});
            skLineSegment(sketch, "E882", {"start": v(59.58, -67.5) * mm, "end": v(66.35, -62.27) * mm});
            skLineSegment(sketch, "E883", {"start": v(66.35, -62.27) * mm, "end": v(67.52, -61.37) * mm});
            skLineSegment(sketch, "E884", {"start": v(67.52, -61.37) * mm, "end": v(67.6, -64.83) * mm});
            skLineSegment(sketch, "E885", {"start": v(67.6, -64.83) * mm, "end": v(67.62, -65.18) * mm});
            skLineSegment(sketch, "E886", {"start": v(14.83, -68.41) * mm, "end": v(14.55, -66.15) * mm});
            skLineSegment(sketch, "E887", {"start": v(14.55, -66.15) * mm, "end": v(14.33, -64.42) * mm});
            skLineSegment(sketch, "E888", {"start": v(14.33, -64.42) * mm, "end": v(14.56, -61.93) * mm});
            skLineSegment(sketch, "E889", {"start": v(14.56, -61.93) * mm, "end": v(14.77, -59.52) * mm});
            skLineSegment(sketch, "E890", {"start": v(66.45, -66.05) * mm, "end": v(66.35, -62.27) * mm});
            skLineSegment(sketch, "E891", {"start": v(66.35, -62.27) * mm, "end": v(66.34, -62) * mm});
            skLineSegment(sketch, "E892", {"start": v(72.79, -59.39) * mm, "end": v(67.6, -64.83) * mm});
            skLineSegment(sketch, "E893", {"start": v(67.6, -64.83) * mm, "end": v(66.45, -66.05) * mm});
            skLineSegment(sketch, "E894", {"start": v(85.7, -50.48) * mm, "end": v(77.35, -52) * mm});
            skLineSegment(sketch, "E895", {"start": v(-923.01, 123.86) * mm, "end": v(-912.2, 123.86) * mm});
            skLineSegment(sketch, "E896", {"start": v(-793.28, 169.64) * mm, "end": v(-656.04, 169.7) * mm});
            skLineSegment(sketch, "E897", {"start": v(405.57, -43.99) * mm, "end": v(408.64, -19.7) * mm});
            skLineSegment(sketch, "E898", {"start": v(404.5, 99.14) * mm, "end": v(393.23, 142.07) * mm});
            skLineSegment(sketch, "E899", {"start": v(410.72, -7.54) * mm, "end": v(413.58, 19.63) * mm});
            skLineSegment(sketch, "E900", {"start": v(408.64, -19.7) * mm, "end": v(412.65, -16.9) * mm});
            skLineSegment(sketch, "E901", {"start": v(431.65, -10.15) * mm, "end": v(420.58, -9.64) * mm});
            skLineSegment(sketch, "E902", {"start": v(431.47, 22.91) * mm, "end": v(449.52, 29.76) * mm});
            skLineSegment(sketch, "E903", {"start": v(449.52, 29.76) * mm, "end": v(452.94, 27.85) * mm});
            skLineSegment(sketch, "E904", {"start": v(452.94, 27.85) * mm, "end": v(455.07, 16.42) * mm});
            skLineSegment(sketch, "E905", {"start": v(413.58, 19.63) * mm, "end": v(431.47, 22.91) * mm});
            skLineSegment(sketch, "E906", {"start": v(464.94, 39.57) * mm, "end": v(465.6, 40.8) * mm});
            skLineSegment(sketch, "E907", {"start": v(408.63, 96.83) * mm, "end": v(404.5, 99.14) * mm});
            skLineSegment(sketch, "E908", {"start": v(368.09, 65.97) * mm, "end": v(367.77, 61.24) * mm});
            skLineSegment(sketch, "E909", {"start": v(272.51, 78.29) * mm, "end": v(270.68, 74.95) * mm});
            skLineSegment(sketch, "E910", {"start": v(268.14, 53.56) * mm, "end": v(266.63, 44.3) * mm});
            skLineSegment(sketch, "E911", {"start": v(303.01, 49.97) * mm, "end": v(300.37, 50.13) * mm});
            skLineSegment(sketch, "E912", {"start": v(275.45, 6.28) * mm, "end": v(277.84, 4.94) * mm});
            skLineSegment(sketch, "E913", {"start": v(297.87, 29.8) * mm, "end": v(299.56, 31.2) * mm});
            skLineSegment(sketch, "E914", {"start": v(299.56, 31.2) * mm, "end": v(304.67, 29.89) * mm});
            skLineSegment(sketch, "E915", {"start": v(376.35, 144.9) * mm, "end": v(374.68, 141.82) * mm});
            skLineSegment(sketch, "E916", {"start": v(372.02, 125.22) * mm, "end": v(368.09, 65.97) * mm});
            skLineSegment(sketch, "E917", {"start": v(278.25, 77.47) * mm, "end": v(274.45, 79.6) * mm});
            skLineSegment(sketch, "E918", {"start": v(285.16, 6.46) * mm, "end": v(297.87, 29.8) * mm});
            skLineSegment(sketch, "E919", {"start": v(332.43, 25.78) * mm, "end": v(361.57, 23.6) * mm});
            skLineSegment(sketch, "E920", {"start": v(361.57, 23.6) * mm, "end": v(366.62, 22.75) * mm});
            skLineSegment(sketch, "E921", {"start": v(368.87, 19.97) * mm, "end": v(370.06, 12.7) * mm});
            skLineSegment(sketch, "E922", {"start": v(304.67, 29.89) * mm, "end": v(332.43, 25.78) * mm});
            skLineSegment(sketch, "E923", {"start": v(370.06, 12.7) * mm, "end": v(374.01, -11.4) * mm});
            skLineSegment(sketch, "E924", {"start": v(412.65, -16.9) * mm, "end": v(434.25, -14.76) * mm});
            skLineSegment(sketch, "E925", {"start": v(413.93, -9.34) * mm, "end": v(410.72, -7.54) * mm});
            skLineSegment(sketch, "E926", {"start": v(420.58, -9.64) * mm, "end": v(413.93, -9.34) * mm});
            skLineSegment(sketch, "E927", {"start": v(460, 13.67) * mm, "end": v(463.4, 19.99) * mm});
            skLineSegment(sketch, "E928", {"start": v(455.07, 16.42) * mm, "end": v(460, 13.67) * mm});
            skLineSegment(sketch, "E929", {"start": v(435.55, -12.33) * mm, "end": v(431.65, -10.15) * mm});
            skLineSegment(sketch, "E930", {"start": v(394.53, -65.46) * mm, "end": v(400.88, -65.04) * mm});
            skLineSegment(sketch, "E931", {"start": v(450.98, 49.7) * mm, "end": v(443.1, 54.1) * mm});
            skLineSegment(sketch, "E932", {"start": v(460.58, 34.82) * mm, "end": v(464.94, 39.57) * mm});
            skLineSegment(sketch, "E933", {"start": v(456.3, 62.97) * mm, "end": v(452.36, 67.67) * mm});
            skLineSegment(sketch, "E934", {"start": v(443.1, 54.1) * mm, "end": v(432.52, 57.31) * mm});
            skLineSegment(sketch, "E935", {"start": v(414.4, 60.5) * mm, "end": v(408, 85.9) * mm});
            skLineSegment(sketch, "E936", {"start": v(419.41, 97.7) * mm, "end": v(408.63, 96.83) * mm});
            skLineSegment(sketch, "E937", {"start": v(459.8, 44.55) * mm, "end": v(456.3, 62.97) * mm});
            skLineSegment(sketch, "E938", {"start": v(452.36, 67.67) * mm, "end": v(448.9, 64.88) * mm});
            skLineSegment(sketch, "E939", {"start": v(462.68, 42.95) * mm, "end": v(459.8, 44.55) * mm});
            skLineSegment(sketch, "E940", {"start": v(448.9, 64.88) * mm, "end": v(450.98, 49.7) * mm});
            skLineSegment(sketch, "E941", {"start": v(410.16, 89.89) * mm, "end": v(425.01, 90.56) * mm});
            skLineSegment(sketch, "E942", {"start": v(431.92, 93.72) * mm, "end": v(431.73, 95.3) * mm});
            skLineSegment(sketch, "E943", {"start": v(423.24, 60.14) * mm, "end": v(414.4, 60.5) * mm});
            skLineSegment(sketch, "E944", {"start": v(425.01, 90.56) * mm, "end": v(431.92, 93.72) * mm});
            skLineSegment(sketch, "E945", {"start": v(431.73, 95.3) * mm, "end": v(424.53, 97.41) * mm});
            skLineSegment(sketch, "E946", {"start": v(424.53, 97.41) * mm, "end": v(419.41, 97.7) * mm});
            skLineSegment(sketch, "E947", {"start": v(408, 85.9) * mm, "end": v(410.16, 89.89) * mm});
            skLineSegment(sketch, "E948", {"start": v(432.52, 57.31) * mm, "end": v(423.24, 60.14) * mm});
            skLineSegment(sketch, "E949", {"start": v(298.07, 50.8) * mm, "end": v(296.25, 52.8) * mm});
            skLineSegment(sketch, "E950", {"start": v(274.45, 79.6) * mm, "end": v(272.51, 78.29) * mm});
            skLineSegment(sketch, "E951", {"start": v(293.7, 57.25) * mm, "end": v(287.49, 68.07) * mm});
            skLineSegment(sketch, "E952", {"start": v(390.36, 146.33) * mm, "end": v(388.45, 147.4) * mm});
            skLineSegment(sketch, "E953", {"start": v(296.25, 52.8) * mm, "end": v(293.7, 57.25) * mm});
            skLineSegment(sketch, "E954", {"start": v(362.59, 57.3) * mm, "end": v(303.01, 49.97) * mm});
            skLineSegment(sketch, "E955", {"start": v(393.23, 142.07) * mm, "end": v(392.4, 145.2) * mm});
            skLineSegment(sketch, "E956", {"start": v(388.45, 147.4) * mm, "end": v(382.29, 146.12) * mm});
            skLineSegment(sketch, "E957", {"start": v(372.64, 138.08) * mm, "end": v(372.02, 125.22) * mm});
            skLineSegment(sketch, "E958", {"start": v(392.4, 145.2) * mm, "end": v(390.36, 146.33) * mm});
            skLineSegment(sketch, "E959", {"start": v(367.77, 61.24) * mm, "end": v(365.74, 57.48) * mm});
            skLineSegment(sketch, "E960", {"start": v(300.37, 50.13) * mm, "end": v(298.07, 50.8) * mm});
            skLineSegment(sketch, "E961", {"start": v(281.87, 75.44) * mm, "end": v(278.25, 77.47) * mm});
            skLineSegment(sketch, "E962", {"start": v(382.29, 146.12) * mm, "end": v(376.35, 144.9) * mm});
            skLineSegment(sketch, "E963", {"start": v(270.68, 74.95) * mm, "end": v(270.72, 69.43) * mm});
            skLineSegment(sketch, "E964", {"start": v(374.68, 141.82) * mm, "end": v(372.64, 138.08) * mm});
            skLineSegment(sketch, "E965", {"start": v(365.74, 57.48) * mm, "end": v(362.59, 57.3) * mm});
            skLineSegment(sketch, "E966", {"start": v(287.49, 68.07) * mm, "end": v(281.87, 75.44) * mm});
            skLineSegment(sketch, "E967", {"start": v(465.6, 40.8) * mm, "end": v(465.2, 41.54) * mm});
            skLineSegment(sketch, "E968", {"start": v(280.91, 2) * mm, "end": v(285.16, 6.46) * mm});
            skLineSegment(sketch, "E969", {"start": v(463.4, 19.99) * mm, "end": v(460.58, 34.82) * mm});
            skLineSegment(sketch, "E970", {"start": v(465.2, 41.54) * mm, "end": v(462.68, 42.95) * mm});
            skLineSegment(sketch, "E971", {"start": v(277.84, 4.94) * mm, "end": v(280.91, 2) * mm});
            skLineSegment(sketch, "E972", {"start": v(404.02, -56.29) * mm, "end": v(405.57, -43.99) * mm});
            skLineSegment(sketch, "E973", {"start": v(270.72, 69.43) * mm, "end": v(268.14, 53.56) * mm});
            skLineSegment(sketch, "E974", {"start": v(266.52, 35.28) * mm, "end": v(269.35, 23.23) * mm});
            skLineSegment(sketch, "E975", {"start": v(434.25, -14.76) * mm, "end": v(435.55, -12.33) * mm});
            skLineSegment(sketch, "E976", {"start": v(366.62, 22.75) * mm, "end": v(368.87, 19.97) * mm});
            skLineSegment(sketch, "E977", {"start": v(382.03, -60.4) * mm, "end": v(385.54, -64.03) * mm});
            skLineSegment(sketch, "E978", {"start": v(385.54, -64.03) * mm, "end": v(394.53, -65.46) * mm});
            skLineSegment(sketch, "E979", {"start": v(266.63, 44.3) * mm, "end": v(262.15, 41.02) * mm});
            skLineSegment(sketch, "E980", {"start": v(262.15, 41.02) * mm, "end": v(266.52, 35.28) * mm});
            skLineSegment(sketch, "E981", {"start": v(269.35, 23.23) * mm, "end": v(271.01, 13.38) * mm});
            skLineSegment(sketch, "E982", {"start": v(273.62, 5.77) * mm, "end": v(275.45, 6.28) * mm});
            skLineSegment(sketch, "E983", {"start": v(271.01, 13.38) * mm, "end": v(273.62, 5.77) * mm});
            skLineSegment(sketch, "E984", {"start": v(374.01, -11.4) * mm, "end": v(382.03, -60.4) * mm});
            skLineSegment(sketch, "E985", {"start": v(400.88, -65.04) * mm, "end": v(404.02, -56.29) * mm});
            skLineSegment(sketch, "E986", {"start": v(-667.83, 83.1) * mm, "end": v(-659.6, 86.56) * mm});
            skLineSegment(sketch, "E987", {"start": v(-651.37, 104.04) * mm, "end": v(-653.05, 112.5) * mm});
            skLineSegment(sketch, "E988", {"start": v(-693.66, 81.93) * mm, "end": v(-689.75, 81.93) * mm});
            skLineSegment(sketch, "E989", {"start": v(-678.9, 81.93) * mm, "end": v(-667.83, 83.1) * mm});
            skLineSegment(sketch, "E990", {"start": v(-689.75, 81.93) * mm, "end": v(-678.9, 81.93) * mm});
            skLineSegment(sketch, "E991", {"start": v(-659.6, 86.56) * mm, "end": v(-654.22, 92.33) * mm});
            skLineSegment(sketch, "E992", {"start": v(-658.2, 118.54) * mm, "end": v(-666.82, 122.16) * mm});
            skLineSegment(sketch, "E993", {"start": v(-653.05, 112.5) * mm, "end": v(-658.2, 118.54) * mm});
            skLineSegment(sketch, "E994", {"start": v(-651.7, 100.4) * mm, "end": v(-651.37, 104.04) * mm});
            skLineSegment(sketch, "E995", {"start": v(-693.35, 123.35) * mm, "end": v(-693.66, 81.93) * mm});
            skLineSegment(sketch, "E996", {"start": v(-654.22, 92.33) * mm, "end": v(-651.7, 100.4) * mm});
            skLineSegment(sketch, "E997", {"start": v(-678.92, 123.36) * mm, "end": v(-693.35, 123.35) * mm});
            skLineSegment(sketch, "E998", {"start": v(-666.82, 122.16) * mm, "end": v(-678.92, 123.36) * mm});
            skLineSegment(sketch, "E999", {"start": v(199.05, 24.57) * mm, "end": v(199.05, 74.08) * mm});
            skFitSpline(sketch, "E1000", {"points": [v(-551.66, -45.2) * mm, v(-478.42, -45.2) * mm, v(-164.35, 24.57) * mm, v(199.05, 24.57) * mm], "startDerivative": vector(280.57, 22.43) * mm, "endDerivative": vector(849.6, -66.57) * mm});
            skFitSpline(sketch, "E1001", {"points": [v(-551.63, 3.62) * mm, v(-478.42, 3.62) * mm, v(-166.47, 74.03) * mm, v(199.05, 74.08) * mm], "startDerivative": vector(325.42, 21.08) * mm, "endDerivative": vector(853.93, -67.4) * mm});
            skLineSegment(sketch, "E1002", {"start": v(-551.66, -45.2) * mm, "end": v(-633.28, -45.2) * mm});
            skLineSegment(sketch, "E1003", {"start": v(-551.63, 3.62) * mm, "end": v(-551.66, -45.2) * mm});
            skSolve(sketch);
        }
        {
            var Q0;
            Q0=makeQuery(id+"F0.imprint","IMPRINT",FACE,{"disambiguationData":[TD([[makeQuery(id+"F0.imprint","IMPRINT",EDGE,{"derivedFrom":sQuery(id+"F0.wireOp",EDGE,"E799")}),-1.0]])]});
            var Q1;
            Q1=makeQuery(id+"F0.imprint","IMPRINT",FACE,{"disambiguationData":[TD([[makeQuery(id+"F0.imprint","IMPRINT",EDGE,{"derivedFrom":sQuery(id+"F0.wireOp",EDGE,"E491")}),-1.0]])]});
            var Q2;
            Q2=makeQuery(id+"F0.imprint","IMPRINT",FACE,{"disambiguationData":[TD([[makeQuery(id+"F0.imprint","IMPRINT",EDGE,{"derivedFrom":sQuery(id+"F0.wireOp",EDGE,"E507")}),-1.0]])]});
            var Q3;
            Q3=makeQuery(id+"F0.imprint","IMPRINT",FACE,{"disambiguationData":[TD([[makeQuery(id+"F0.imprint","IMPRINT",EDGE,{"derivedFrom":sQuery(id+"F0.wireOp",EDGE,"E511")}),-1.0]])]});
            extrude(context, id + "F1", {"entities" : qUnion([Q0, Q1, Q2, Q3]), "depth" : 25 * mm, "offsetDistance" : 25 * mm});
        }
    });
